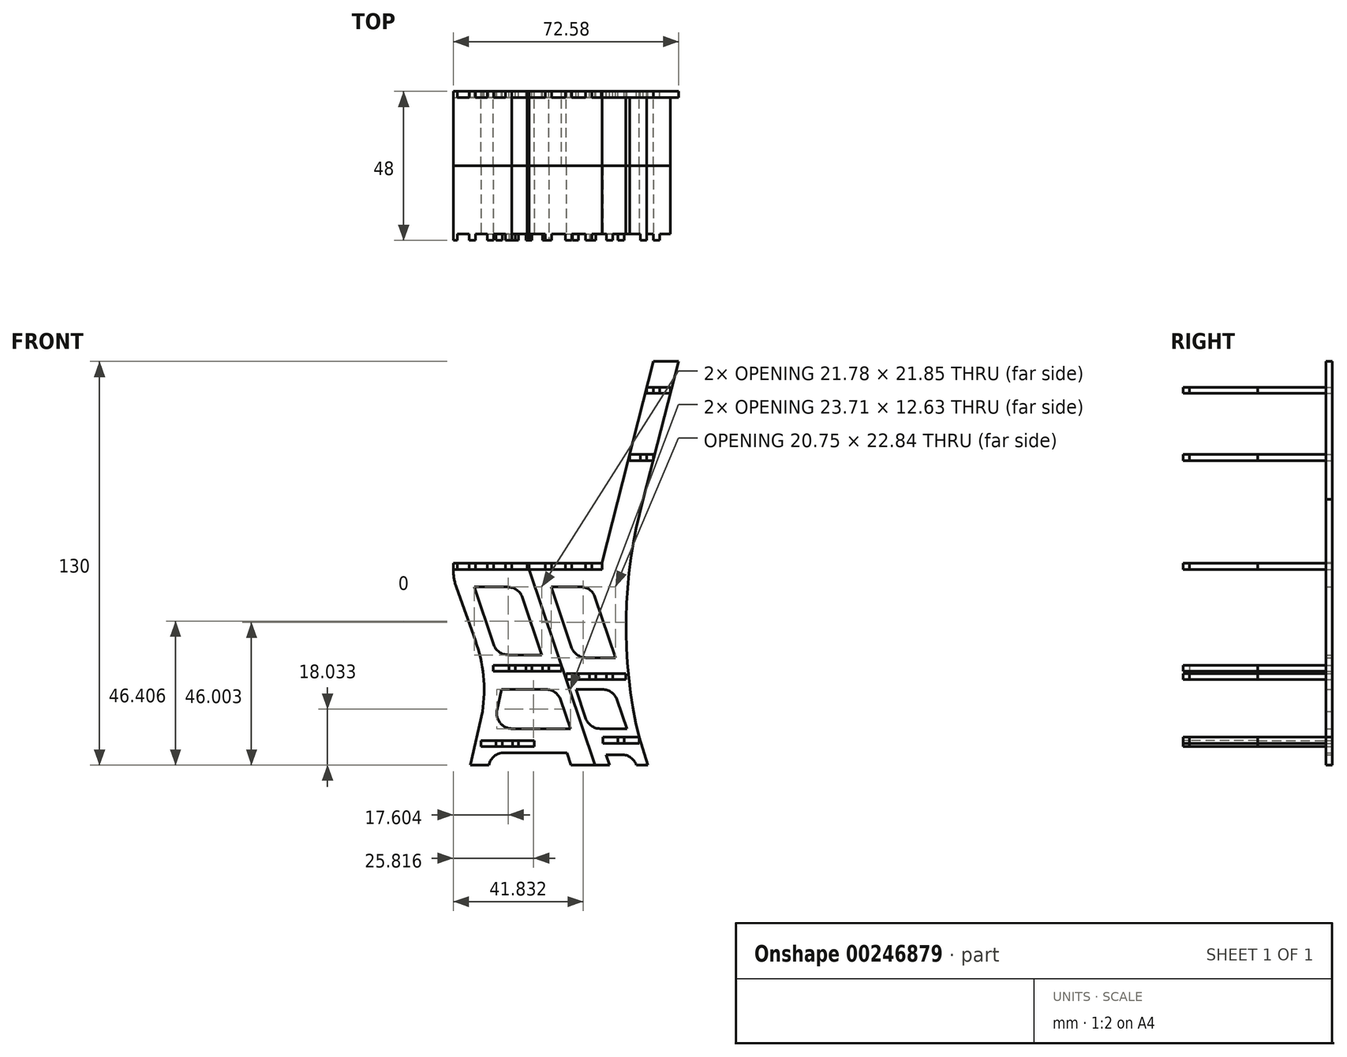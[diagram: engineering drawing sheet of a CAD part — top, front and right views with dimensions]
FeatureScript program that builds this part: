
annotation { "Feature Type Name" : "Feature", "Feature Type Description" : "" }
export const myFeature = defineFeature(function(context is Context, id is Id, definition is map)
    precondition{}
    {
        {
            var Q0;
            Q0=qCreatedBy(makeId("Front.planeOp"),FACE);
            var sketch = newSketch(context, id + "F0", { "sketchPlane" : qUnion([Q0])});
            skLineSegment(sketch, "E0", {"start": v(104.8, -15.97) * mm, "end": v(120.66, 46.4) * mm});
            skLineSegment(sketch, "E1", {"start": v(120.66, 46.4) * mm, "end": v(128.86, 46.4) * mm});
            skLineSegment(sketch, "E2", {"start": v(128.86, 46.4) * mm, "end": v(116.21, -2.66) * mm});
            skLineSegment(sketch, "E3", {"start": v(116.07, -74.61) * mm, "end": v(119.28, -84.78) * mm});
            skLineSegment(sketch, "E4", {"start": v(126.58, -83.6) * mm, "end": v(61.72, -83.6) * mm});
            skLineSegment(sketch, "E5", {"start": v(61.72, -83.6) * mm, "end": v(65.63, -66.38) * mm});
            skLineSegment(sketch, "E6", {"start": v(63.65, -44.37) * mm, "end": v(57.26, -26.44) * mm});
            skLineSegment(sketch, "E7", {"start": v(80.01, -18.6) * mm, "end": v(101.88, -83.6) * mm});
            skLineSegment(sketch, "E8.bottom", {"start": v(74.23, -51.43) * mm, "end": v(76.23, -51.43) * mm});
            skLineSegment(sketch, "E8.top", {"start": v(74.23, -53.43) * mm, "end": v(76.23, -53.43) * mm});
            skLineSegment(sketch, "E8.left", {"start": v(74.23, -51.43) * mm, "end": v(74.23, -53.43) * mm});
            skLineSegment(sketch, "E8.right", {"start": v(76.23, -51.43) * mm, "end": v(76.23, -53.43) * mm});
            skLineSegment(sketch, "E9.1.0.0", {"start": v(79.63, -53.43) * mm, "end": v(81.63, -53.43) * mm});
            skLineSegment(sketch, "E9.1.0.1", {"start": v(79.63, -51.43) * mm, "end": v(79.63, -53.43) * mm});
            skLineSegment(sketch, "E9.1.0.2", {"start": v(79.63, -51.43) * mm, "end": v(81.63, -51.43) * mm});
            skLineSegment(sketch, "E9.1.0.3", {"start": v(81.63, -51.43) * mm, "end": v(81.63, -53.43) * mm});
            skLineSegment(sketch, "E9.2.0.0", {"start": v(85.03, -53.43) * mm, "end": v(87.03, -53.43) * mm});
            skLineSegment(sketch, "E9.2.0.1", {"start": v(85.03, -51.43) * mm, "end": v(85.03, -53.43) * mm});
            skLineSegment(sketch, "E9.2.0.2", {"start": v(85.03, -51.43) * mm, "end": v(87.03, -51.43) * mm});
            skLineSegment(sketch, "E9.2.0.3", {"start": v(87.03, -51.43) * mm, "end": v(87.03, -53.43) * mm});
            skLineSegment(sketch, "E9.direction1", {"start": v(74.23, -53.43) * mm, "end": v(79.63, -53.43) * mm, "construction": true});
            skLineSegment(sketch, "E10.left", {"start": v(94.61, -54.11) * mm, "end": v(94.61, -56.11) * mm});
            skLineSegment(sketch, "E10.right", {"start": v(96.61, -54.11) * mm, "end": v(96.61, -56.11) * mm});
            skLineSegment(sketch, "E11.bottom", {"start": v(69.98, -75.7) * mm, "end": v(71.98, -75.7) * mm});
            skLineSegment(sketch, "E11.top", {"start": v(69.98, -77.7) * mm, "end": v(71.98, -77.7) * mm});
            skLineSegment(sketch, "E11.left", {"start": v(69.98, -75.7) * mm, "end": v(69.98, -77.7) * mm});
            skLineSegment(sketch, "E11.right", {"start": v(71.98, -75.7) * mm, "end": v(71.98, -77.7) * mm});
            skLineSegment(sketch, "E12.1.0.0", {"start": v(75.28, -75.7) * mm, "end": v(75.28, -77.7) * mm});
            skLineSegment(sketch, "E12.1.0.1", {"start": v(75.28, -75.7) * mm, "end": v(77.28, -75.7) * mm});
            skLineSegment(sketch, "E12.1.0.2", {"start": v(77.28, -75.7) * mm, "end": v(77.28, -77.7) * mm});
            skLineSegment(sketch, "E12.1.0.3", {"start": v(75.28, -77.7) * mm, "end": v(77.28, -77.7) * mm});
            skLineSegment(sketch, "E12.direction1", {"start": v(69.98, -77.7) * mm, "end": v(75.28, -77.7) * mm, "construction": true});
            skLineSegment(sketch, "E13.bottom", {"start": v(109.26, -74.61) * mm, "end": v(111.26, -74.61) * mm});
            skLineSegment(sketch, "E13.top", {"start": v(109.26, -76.61) * mm, "end": v(111.26, -76.61) * mm});
            skLineSegment(sketch, "E14.1.0.0", {"start": v(100.11, -54.11) * mm, "end": v(100.11, -56.11) * mm});
            skLineSegment(sketch, "E14.1.0.1", {"start": v(102.11, -54.11) * mm, "end": v(102.11, -56.11) * mm});
            skLineSegment(sketch, "E14.1.0.2", {"start": v(92.81, -56.11) * mm, "end": v(94.81, -56.11) * mm});
            skLineSegment(sketch, "E14.1.0.3", {"start": v(92.81, -54.11) * mm, "end": v(94.81, -54.11) * mm});
            skLineSegment(sketch, "E14.2.0.0", {"start": v(105.61, -54.11) * mm, "end": v(105.61, -56.11) * mm});
            skLineSegment(sketch, "E14.2.0.1", {"start": v(107.61, -54.11) * mm, "end": v(107.61, -56.11) * mm});
            skLineSegment(sketch, "E14.2.0.2", {"start": v(98.31, -56.11) * mm, "end": v(100.31, -56.11) * mm});
            skLineSegment(sketch, "E14.2.0.3", {"start": v(98.31, -54.11) * mm, "end": v(100.31, -54.11) * mm});
            skLineSegment(sketch, "E15.1.0.1", {"start": v(55.63, -20.6) * mm, "end": v(57.63, -20.6) * mm});
            skLineSegment(sketch, "E15.1.0.2", {"start": v(57.63, -18.6) * mm, "end": v(57.63, -20.6) * mm});
            skLineSegment(sketch, "E15.2.0.0", {"start": v(61.43, -18.6) * mm, "end": v(61.43, -20.6) * mm});
            skLineSegment(sketch, "E15.2.0.1", {"start": v(61.43, -20.6) * mm, "end": v(63.43, -20.6) * mm});
            skLineSegment(sketch, "E15.2.0.2", {"start": v(63.43, -18.6) * mm, "end": v(63.43, -20.6) * mm});
            skLineSegment(sketch, "E15.3.0.0", {"start": v(67.23, -18.6) * mm, "end": v(67.23, -20.6) * mm});
            skLineSegment(sketch, "E15.3.0.1", {"start": v(67.23, -20.6) * mm, "end": v(69.23, -20.6) * mm});
            skLineSegment(sketch, "E15.3.0.2", {"start": v(69.23, -18.6) * mm, "end": v(69.23, -20.6) * mm});
            skLineSegment(sketch, "E16.bottom", {"start": v(73.03, -18.6) * mm, "end": v(75.03, -18.6) * mm});
            skLineSegment(sketch, "E16.top", {"start": v(73.03, -20.6) * mm, "end": v(75.03, -20.6) * mm});
            skLineSegment(sketch, "E16.left", {"start": v(73.03, -18.6) * mm, "end": v(73.03, -20.6) * mm});
            skLineSegment(sketch, "E16.right", {"start": v(75.03, -18.6) * mm, "end": v(75.03, -20.6) * mm});
            skLineSegment(sketch, "E17.1.0.1", {"start": v(79.48, -20.6) * mm, "end": v(81.48, -20.6) * mm});
            skLineSegment(sketch, "E17.2.0.0", {"start": v(85.94, -18.6) * mm, "end": v(85.94, -20.6) * mm});
            skLineSegment(sketch, "E17.2.0.1", {"start": v(85.94, -20.6) * mm, "end": v(87.94, -20.6) * mm});
            skLineSegment(sketch, "E17.2.0.2", {"start": v(87.94, -18.6) * mm, "end": v(87.94, -20.6) * mm});
            skLineSegment(sketch, "E17.3.0.0", {"start": v(92.4, -18.6) * mm, "end": v(92.4, -20.6) * mm});
            skLineSegment(sketch, "E17.3.0.1", {"start": v(92.4, -20.6) * mm, "end": v(94.4, -20.6) * mm});
            skLineSegment(sketch, "E17.3.0.2", {"start": v(94.4, -18.6) * mm, "end": v(94.4, -20.6) * mm});
            skLineSegment(sketch, "E17.4.0.0", {"start": v(98.85, -18.6) * mm, "end": v(98.85, -20.6) * mm});
            skLineSegment(sketch, "E17.4.0.1", {"start": v(98.85, -20.6) * mm, "end": v(100.85, -20.6) * mm});
            skLineSegment(sketch, "E17.4.0.2", {"start": v(100.85, -18.57) * mm, "end": v(100.85, -20.6) * mm});
            skLineSegment(sketch, "E17.direction1", {"start": v(73.03, -20.6) * mm, "end": v(79.48, -20.6) * mm, "construction": true});
            skPoint(sketch, "E18.visualSharp", {"position": v(104.13, -18.6) * mm});
            skArc(sketch, "E18.filletArc", {"start": v(100.24, -18.6) * mm, "mid": v(100.55, -18.6) * mm, "end": v(100.85, -18.57) * mm});
            skPoint(sketch, "E19.orphan", {"position": v(100.85, -18.6) * mm});
            skLineSegment(sketch, "E20.bottom", {"start": v(116.51, 16.45) * mm, "end": v(118.51, 16.45) * mm, "construction": true});
            skLineSegment(sketch, "E20.top", {"start": v(116.51, 14.45) * mm, "end": v(118.51, 14.45) * mm, "construction": true});
            skLineSegment(sketch, "E20.left", {"start": v(116.51, 16.45) * mm, "end": v(116.51, 14.45) * mm});
            skLineSegment(sketch, "E20.right", {"start": v(118.51, 16.45) * mm, "end": v(118.51, 14.45) * mm});
            skLineSegment(sketch, "E21.bottom", {"start": v(120.66, 38.08) * mm, "end": v(122.66, 38.08) * mm});
            skLineSegment(sketch, "E21.top", {"start": v(120.66, 36.08) * mm, "end": v(122.66, 36.08) * mm});
            skLineSegment(sketch, "E21.left", {"start": v(120.66, 38.08) * mm, "end": v(120.66, 36.08) * mm});
            skLineSegment(sketch, "E21.right", {"start": v(122.66, 38.08) * mm, "end": v(122.66, 36.08) * mm});
            skLineSegment(sketch, "E22", {"start": v(55.18, -20.6) * mm, "end": v(104.13, -20.6) * mm});
            skLineSegment(sketch, "E23", {"start": v(104.13, -20.6) * mm, "end": v(104.13, -18.6) * mm});
            skLineSegment(sketch, "E24", {"start": v(100.24, -18.6) * mm, "end": v(104.13, -18.6) * mm});
            skLineSegment(sketch, "E25", {"start": v(91.06, -51.43) * mm, "end": v(74.23, -51.43) * mm});
            skLineSegment(sketch, "E26", {"start": v(69.09, -53.43) * mm, "end": v(91.06, -53.43) * mm});
            skLineSegment(sketch, "E27", {"start": v(92.63, -54.11) * mm, "end": v(111.76, -54.11) * mm});
            skLineSegment(sketch, "E28", {"start": v(92.63, -56.11) * mm, "end": v(111.76, -56.11) * mm});
            skLineSegment(sketch, "E29.bottom", {"start": v(65.2, -75.7) * mm, "end": v(82.27, -75.7) * mm});
            skLineSegment(sketch, "E29.top", {"start": v(65.2, -77.7) * mm, "end": v(82.27, -77.7) * mm});
            skLineSegment(sketch, "E29.left", {"start": v(65.2, -75.7) * mm, "end": v(65.2, -77.7) * mm});
            skLineSegment(sketch, "E29.right", {"start": v(82.27, -75.7) * mm, "end": v(82.27, -77.7) * mm});
            skLineSegment(sketch, "E30", {"start": v(69.09, -51.43) * mm, "end": v(69.09, -53.43) * mm});
            skLineSegment(sketch, "E31", {"start": v(111.76, -54.11) * mm, "end": v(111.76, -56.11) * mm});
            skLineSegment(sketch, "E32", {"start": v(116.07, -74.61) * mm, "end": v(104.49, -74.61) * mm});
            skPoint(sketch, "E32.endSnap0", {"position": v(110.26, -74.61) * mm});
            skLineSegment(sketch, "E33", {"start": v(104.49, -74.61) * mm, "end": v(104.49, -76.61) * mm});
            skLineSegment(sketch, "E34", {"start": v(104.49, -76.61) * mm, "end": v(116.07, -76.61) * mm});
            skLineSegment(sketch, "E35", {"start": v(74.23, -51.43) * mm, "end": v(69.09, -51.43) * mm});
            skPoint(sketch, "E36.orphan", {"position": v(59.58, -53.43) * mm});
            skLineSegment(sketch, "E37", {"start": v(108.48, -49.03) * mm, "end": v(99.02, -49.03) * mm});
            skLineSegment(sketch, "E38", {"start": v(94.28, -45.62) * mm, "end": v(87.74, -26.18) * mm});
            skLineSegment(sketch, "E39", {"start": v(87.74, -26.18) * mm, "end": v(97.2, -26.18) * mm});
            skLineSegment(sketch, "E40", {"start": v(101.94, -29.59) * mm, "end": v(108.48, -49.03) * mm});
            skPoint(sketch, "E41.visualSharp", {"position": v(100.8, -26.18) * mm});
            skArc(sketch, "E41.filletArc", {"start": v(101.94, -29.59) * mm, "mid": v(100.12, -27.12) * mm, "end": v(97.2, -26.18) * mm});
            skPoint(sketch, "E42.visualSharp", {"position": v(95.43, -49.03) * mm});
            skArc(sketch, "E42.filletArc", {"start": v(94.28, -45.62) * mm, "mid": v(96.1, -48.09) * mm, "end": v(99.02, -49.03) * mm});
            skLineSegment(sketch, "E43", {"start": v(84.77, -48.13) * mm, "end": v(73.94, -48.13) * mm});
            skLineSegment(sketch, "E44", {"start": v(69.2, -44.72) * mm, "end": v(63, -26.28) * mm});
            skLineSegment(sketch, "E45", {"start": v(63, -26.28) * mm, "end": v(73.83, -26.28) * mm});
            skLineSegment(sketch, "E46", {"start": v(78.57, -29.69) * mm, "end": v(84.77, -48.13) * mm});
            skArc(sketch, "E47.filletArc", {"start": v(78.57, -29.69) * mm, "mid": v(76.75, -27.22) * mm, "end": v(73.83, -26.28) * mm});
            skArc(sketch, "E48.filletArc", {"start": v(69.2, -44.72) * mm, "mid": v(71.02, -47.19) * mm, "end": v(73.94, -48.13) * mm});
            skLineSegment(sketch, "E49", {"start": v(110.48, -80.26) * mm, "end": v(105.45, -80.26) * mm});
            skLineSegment(sketch, "E50", {"start": v(105.45, -80.26) * mm, "end": v(106.64, -83.6) * mm});
            skPoint(sketch, "E51.visualSharp", {"position": v(111.89, -80.26) * mm});
            skArc(sketch, "E51.filletArc", {"start": v(115.43, -85.97) * mm, "mid": v(114.26, -81.98) * mm, "end": v(110.48, -80.26) * mm});
            skLineSegment(sketch, "E52", {"start": v(95.75, -59.26) * mm, "end": v(104.29, -59.26) * mm});
            skArc(sketch, "E53.filletArc", {"start": v(109.03, -62.67) * mm, "mid": v(107.2, -60.2) * mm, "end": v(104.29, -59.26) * mm});
            skLineSegment(sketch, "E54", {"start": v(112.13, -71.9) * mm, "end": v(103.59, -71.9) * mm});
            skLineSegment(sketch, "E55", {"start": v(109.03, -62.67) * mm, "end": v(112.13, -71.9) * mm});
            skLineSegment(sketch, "E56", {"start": v(98.85, -68.49) * mm, "end": v(95.75, -59.26) * mm});
            skPoint(sketch, "E57.visualSharp", {"position": v(100, -71.9) * mm});
            skArc(sketch, "E57.filletArc", {"start": v(98.85, -68.49) * mm, "mid": v(100.67, -70.95) * mm, "end": v(103.59, -71.9) * mm});
            skLineSegment(sketch, "E58", {"start": v(92.81, -79.65) * mm, "end": v(72.62, -79.65) * mm});
            skLineSegment(sketch, "E59", {"start": v(92.81, -79.65) * mm, "end": v(94.15, -83.6) * mm});
            skPoint(sketch, "E60.visualSharp", {"position": v(60.32, -80.23) * mm});
            skArc(sketch, "E60.filletArc", {"start": v(72.62, -79.65) * mm, "mid": v(69.47, -80.76) * mm, "end": v(67.73, -83.6) * mm});
            skLineSegment(sketch, "E61", {"start": v(93.95, -71.9) * mm, "end": v(75.24, -71.9) * mm});
            skLineSegment(sketch, "E62", {"start": v(86.1, -59.26) * mm, "end": v(71.85, -59.26) * mm});
            skLineSegment(sketch, "E63", {"start": v(71.85, -59.26) * mm, "end": v(70.37, -65.78) * mm});
            skLineSegment(sketch, "E64", {"start": v(93.95, -71.9) * mm, "end": v(90.85, -62.67) * mm});
            skPoint(sketch, "E65.visualSharp", {"position": v(82.4, -59.26) * mm});
            skArc(sketch, "E65.filletArc", {"start": v(90.85, -62.67) * mm, "mid": v(89.03, -60.2) * mm, "end": v(86.1, -59.26) * mm});
            skPoint(sketch, "E66.visualSharp", {"position": v(61.68, -71.9) * mm});
            skArc(sketch, "E66.filletArc", {"start": v(70.37, -65.78) * mm, "mid": v(71.33, -70.01) * mm, "end": v(75.24, -71.9) * mm});
            skLineSegment(sketch, "E67", {"start": v(92.63, -56.11) * mm, "end": v(92.63, -54.11) * mm});
            skLineSegment(sketch, "E68", {"start": v(91.06, -51.43) * mm, "end": v(91.06, -53.43) * mm});
            skPoint(sketch, "E69.orphan", {"position": v(91.96, -54.11) * mm});
            skLineSegment(sketch, "E70", {"start": v(116.07, -74.61) * mm, "end": v(116.07, -76.61) * mm});
            skLineSegment(sketch, "E71", {"start": v(120.88, 15.45) * mm, "end": v(112.8, 15.45) * mm, "construction": true});
            skPoint(sketch, "E71.startSnap0", {"position": v(118.51, 15.45) * mm});
            skLineSegment(sketch, "E72.bottom", {"start": v(120.62, 14.45) * mm, "end": v(113.05, 14.45) * mm});
            skLineSegment(sketch, "E72.top", {"start": v(120.62, 16.45) * mm, "end": v(113.05, 16.45) * mm});
            skLineSegment(sketch, "E72.left", {"start": v(120.62, 14.45) * mm, "end": v(120.62, 16.45) * mm});
            skLineSegment(sketch, "E72.right", {"start": v(113.05, 14.45) * mm, "end": v(113.05, 16.45) * mm});
            skPoint(sketch, "E73.oppositeSnap0", {"position": v(121.66, 38.08) * mm});
            skLineSegment(sketch, "E73.bottom", {"start": v(126.2, 36.08) * mm, "end": v(118.55, 36.08) * mm});
            skLineSegment(sketch, "E73.top", {"start": v(126.2, 38.08) * mm, "end": v(118.55, 38.08) * mm});
            skLineSegment(sketch, "E73.left", {"start": v(126.2, 36.08) * mm, "end": v(126.2, 38.08) * mm});
            skLineSegment(sketch, "E73.right", {"start": v(118.55, 36.08) * mm, "end": v(118.55, 38.08) * mm});
            skLineSegment(sketch, "E74", {"start": v(111.26, -74.61) * mm, "end": v(111.26, -76.61) * mm});
            skLineSegment(sketch, "E75", {"start": v(109.26, -74.61) * mm, "end": v(109.26, -76.61) * mm});
            skPoint(sketch, "E76.orphan", {"position": v(100, -84.78) * mm});
            skArc(sketch, "E77", {"start": v(117.4, 1.97) * mm, "mid": v(111.92, -36.24) * mm, "end": v(116.07, -74.61) * mm});
            skPoint(sketch, "E78.orphan", {"position": v(105.95, -42.46) * mm});
            skArc(sketch, "E79", {"start": v(65.63, -66.38) * mm, "mid": v(65.94, -54.82) * mm, "end": v(63.36, -43.54) * mm});
            skLineSegment(sketch, "E80.trimOffspring", {"start": v(54.47, -18.6) * mm, "end": v(100.24, -18.6) * mm});
            skLineSegment(sketch, "E81.trimOffspring", {"start": v(55.18, -20.6) * mm, "end": v(55.63, -20.6) * mm, "construction": true});
            skPoint(sketch, "E82.start.orphan", {"position": v(47.88, -20.6) * mm});
            skPoint(sketch, "E83.start.orphan", {"position": v(41.93, -18.6) * mm});
            skPoint(sketch, "E84.top.start.orphan", {"position": v(49.83, -20.6) * mm});
            skLineSegment(sketch, "E85", {"start": v(80.68, -20.6) * mm, "end": v(80.68, -18.6) * mm});
            skLineSegment(sketch, "E86", {"start": v(80.01, -18.6) * mm, "end": v(80.01, -20.6) * mm});
            skLineSegment(sketch, "E87", {"start": v(56.28, -18.6) * mm, "end": v(56.28, -20.74) * mm});
            skLineSegment(sketch, "E88", {"start": v(104.8, -15.97) * mm, "end": v(104.2, -18.33) * mm});
            skArc(sketch, "E89", {"start": v(103.91, -18.6) * mm, "mid": v(104.1, -18.49) * mm, "end": v(104.21, -18.28) * mm});
            skPoint(sketch, "E90.newPointB", {"position": v(54.47, -18.6) * mm});
            skArc(sketch, "E90.filletArc", {"start": v(56.28, -20.74) * mm, "mid": v(56.52, -23.63) * mm, "end": v(57.26, -26.44) * mm});
            skSolve(sketch);
        }
        {
            var Q0;
            {var subQ12=sQuery(id+"F0.wireOp",EDGE,"E5");Q0=makeQuery(id+"F0.imprint","IMPRINT",FACE,{"disambiguationData":[TD([[makeQuery(id+"F0.imprint","IMPRINT",EDGE,{"derivedFrom":subQ12}),-1.0]])]});}
            var Q1;
            {var subQ3=sQuery(id+"F0.wireOp",EDGE,"E84.left");Q1=makeQuery(id+"F0.imprint","IMPRINT",FACE,{"disambiguationData":[TD([[makeQuery(id+"F0.imprint","IMPRINT",EDGE,{"derivedFrom":subQ3}),-1.0]])]});}
            var Q2;
            {var subQ0=sQuery(id+"F0.wireOp",EDGE,"E84.right");Q2=makeQuery(id+"F0.imprint","IMPRINT",FACE,{"disambiguationData":[TD([[makeQuery(id+"F0.imprint","IMPRINT",EDGE,{"derivedFrom":subQ0}),1.0]])]});}
            var Q3;
            {var subQ0=sQuery(id+"F0.wireOp",EDGE,"E15.1.0.2");Q3=makeQuery(id+"F0.imprint","IMPRINT",FACE,{"disambiguationData":[TD([[makeQuery(id+"F0.imprint","IMPRINT",EDGE,{"derivedFrom":subQ0}),1.0]])]});}
            var Q4;
            {var subQ0=sQuery(id+"F0.wireOp",EDGE,"E15.2.0.2");Q4=makeQuery(id+"F0.imprint","IMPRINT",FACE,{"disambiguationData":[TD([[makeQuery(id+"F0.imprint","IMPRINT",EDGE,{"derivedFrom":subQ0}),1.0]])]});}
            var Q5;
            {var subQ3=sQuery(id+"F0.wireOp",EDGE,"E15.3.0.2");Q5=makeQuery(id+"F0.imprint","IMPRINT",FACE,{"disambiguationData":[TD([[makeQuery(id+"F0.imprint","IMPRINT",EDGE,{"derivedFrom":subQ3}),1.0]])]});}
            var Q6;
            {var subQ0=sQuery(id+"F0.wireOp",EDGE,"E8.left");Q6=makeQuery(id+"F0.imprint","IMPRINT",FACE,{"disambiguationData":[TD([[makeQuery(id+"F0.imprint","IMPRINT",EDGE,{"derivedFrom":subQ0}),-1.0]])]});}
            var Q7;
            {var subQ0=sQuery(id+"F0.wireOp",EDGE,"E8.right");Q7=makeQuery(id+"F0.imprint","IMPRINT",FACE,{"disambiguationData":[TD([[makeQuery(id+"F0.imprint","IMPRINT",EDGE,{"derivedFrom":subQ0}),1.0]])]});}
            var Q8;
            {var subQ0=sQuery(id+"F0.wireOp",EDGE,"E9.1.0.3");Q8=makeQuery(id+"F0.imprint","IMPRINT",FACE,{"disambiguationData":[TD([[makeQuery(id+"F0.imprint","IMPRINT",EDGE,{"derivedFrom":subQ0}),1.0]])]});}
            var Q9;
            {var subQ0=sQuery(id+"F0.wireOp",EDGE,"E9.2.0.3");Q9=makeQuery(id+"F0.imprint","IMPRINT",FACE,{"disambiguationData":[TD([[makeQuery(id+"F0.imprint","IMPRINT",EDGE,{"derivedFrom":subQ0}),1.0]])]});}
            var Q10;
            {var subQ0=sQuery(id+"F0.wireOp",EDGE,"E12.1.0.2");Q10=makeQuery(id+"F0.imprint","IMPRINT",FACE,{"disambiguationData":[TD([[makeQuery(id+"F0.imprint","IMPRINT",EDGE,{"derivedFrom":subQ0}),1.0]])]});}
            var Q11;
            {var subQ0=sQuery(id+"F0.wireOp",EDGE,"E11.right");Q11=makeQuery(id+"F0.imprint","IMPRINT",FACE,{"disambiguationData":[TD([[makeQuery(id+"F0.imprint","IMPRINT",EDGE,{"derivedFrom":subQ0}),1.0]])]});}
            var Q12;
            {var subQ0=sQuery(id+"F0.wireOp",EDGE,"E11.left");Q12=makeQuery(id+"F0.imprint","IMPRINT",FACE,{"disambiguationData":[TD([[makeQuery(id+"F0.imprint","IMPRINT",EDGE,{"derivedFrom":subQ0}),-1.0]])]});}
            var Q13;
            {var subQ0=sQuery(id+"F0.wireOp",EDGE,"E16.right");Q13=makeQuery(id+"F0.imprint","IMPRINT",FACE,{"disambiguationData":[TD([[makeQuery(id+"F0.imprint","IMPRINT",EDGE,{"derivedFrom":subQ0}),1.0]])]});}
            extrude(context, id + "F1", {"entities" : qUnion([Q0, Q1, Q2, Q3, Q4, Q5, Q6, Q7, Q8, Q9, Q10, Q11, Q12, Q13]), "depth" : 2 * mm});
        }
        {
            var Q0;
            {var subQ1=sQuery(id+"F0.wireOp",EDGE,"E0");Q0=makeQuery(id+"F0.imprint","IMPRINT",FACE,{"disambiguationData":[TD([[makeQuery(id+"F0.imprint","IMPRINT",EDGE,{"derivedFrom":subQ1}),-1.0]])]});}
            var Q1;
            {var subQ3=sQuery(id+"F0.wireOp",EDGE,"E16.left");Q1=makeQuery(id+"F0.imprint","IMPRINT",FACE,{"disambiguationData":[TD([[makeQuery(id+"F0.imprint","IMPRINT",EDGE,{"derivedFrom":subQ3}),-1.0]])]});}
            var Q2;
            {var subQ0=sQuery(id+"F0.wireOp",EDGE,"E17.1.0.2");Q2=makeQuery(id+"F0.imprint","IMPRINT",FACE,{"disambiguationData":[TD([[makeQuery(id+"F0.imprint","IMPRINT",EDGE,{"derivedFrom":subQ0}),1.0]])]});}
            var Q3;
            {var subQ0=sQuery(id+"F0.wireOp",EDGE,"E17.2.0.2");Q3=makeQuery(id+"F0.imprint","IMPRINT",FACE,{"disambiguationData":[TD([[makeQuery(id+"F0.imprint","IMPRINT",EDGE,{"derivedFrom":subQ0}),1.0]])]});}
            var Q4;
            {var subQ0=sQuery(id+"F0.wireOp",EDGE,"E17.3.0.2");Q4=makeQuery(id+"F0.imprint","IMPRINT",FACE,{"disambiguationData":[TD([[makeQuery(id+"F0.imprint","IMPRINT",EDGE,{"derivedFrom":subQ0}),1.0]])]});}
            var Q5;
            {var subQ5=sQuery(id+"F0.wireOp",EDGE,"E23");Q5=makeQuery(id+"F0.imprint","IMPRINT",FACE,{"disambiguationData":[TD([[makeQuery(id+"F0.imprint","IMPRINT",EDGE,{"derivedFrom":subQ5}),1.0]])]});}
            var Q6;
            {var subQ1=sQuery(id+"F0.wireOp",EDGE,"E10.left");Q6=makeQuery(id+"F0.imprint","IMPRINT",FACE,{"disambiguationData":[TD([[makeQuery(id+"F0.imprint","IMPRINT",EDGE,{"derivedFrom":subQ1}),-1.0]])]});}
            var Q7;
            {var subQ0=sQuery(id+"F0.wireOp",EDGE,"E10.right");Q7=makeQuery(id+"F0.imprint","IMPRINT",FACE,{"disambiguationData":[TD([[makeQuery(id+"F0.imprint","IMPRINT",EDGE,{"derivedFrom":subQ0}),1.0]])]});}
            var Q8;
            {var subQ0=sQuery(id+"F0.wireOp",EDGE,"E14.1.0.1");Q8=makeQuery(id+"F0.imprint","IMPRINT",FACE,{"disambiguationData":[TD([[makeQuery(id+"F0.imprint","IMPRINT",EDGE,{"derivedFrom":subQ0}),1.0]])]});}
            var Q9;
            {var subQ0=sQuery(id+"F0.wireOp",EDGE,"E14.2.0.1");Q9=makeQuery(id+"F0.imprint","IMPRINT",FACE,{"disambiguationData":[TD([[makeQuery(id+"F0.imprint","IMPRINT",EDGE,{"derivedFrom":subQ0}),1.0]])]});}
            var Q10;
            {var subQ0=sQuery(id+"F0.wireOp",EDGE,"E13.left");Q10=makeQuery(id+"F0.imprint","IMPRINT",FACE,{"disambiguationData":[TD([[makeQuery(id+"F0.imprint","IMPRINT",EDGE,{"derivedFrom":subQ0}),-1.0]])]});}
            var Q11;
            {var subQ5=sQuery(id+"F0.wireOp",EDGE,"E13.right");Q11=makeQuery(id+"F0.imprint","IMPRINT",FACE,{"disambiguationData":[TD([[makeQuery(id+"F0.imprint","IMPRINT",EDGE,{"derivedFrom":subQ5}),1.0]])]});}
            var Q12;
            {var subQ59=sQuery(id+"F0.wireOp",EDGE,"E16.top");Q12=makeQuery(id+"F0.imprint","IMPRINT",FACE,{"disambiguationData":[TD([[makeQuery(id+"F0.imprint","IMPRINT",EDGE,{"derivedFrom":subQ59}),-1.0]])]});}
            var Q13;
            {var subQ0=sQuery(id+"F0.wireOp",EDGE,"E21.right");Q13=makeQuery(id+"F0.imprint","IMPRINT",FACE,{"disambiguationData":[TD([[makeQuery(id+"F0.imprint","IMPRINT",EDGE,{"derivedFrom":subQ0}),1.0]])]});}
            var Q14;
            {var subQ0=sQuery(id+"F0.wireOp",EDGE,"E21.left");Q14=makeQuery(id+"F0.imprint","IMPRINT",FACE,{"disambiguationData":[TD([[makeQuery(id+"F0.imprint","IMPRINT",EDGE,{"derivedFrom":subQ0}),-1.0]])]});}
            var Q15;
            {var subQ3=sQuery(id+"F0.wireOp",EDGE,"E72.left");Q15=makeQuery(id+"F0.imprint","IMPRINT",FACE,{"disambiguationData":[TD([[makeQuery(id+"F0.imprint","IMPRINT",EDGE,{"derivedFrom":subQ3}),-1.0]])]});}
            var Q16;
            {var subQ0=sQuery(id+"F0.wireOp",EDGE,"E20.right");Q16=makeQuery(id+"F0.imprint","IMPRINT",FACE,{"disambiguationData":[TD([[makeQuery(id+"F0.imprint","IMPRINT",EDGE,{"derivedFrom":subQ0}),1.0]])]});}
            var Q17;
            {var subQ0=sQuery(id+"F0.wireOp",EDGE,"E20.left");Q17=makeQuery(id+"F0.imprint","IMPRINT",FACE,{"disambiguationData":[TD([[makeQuery(id+"F0.imprint","IMPRINT",EDGE,{"derivedFrom":subQ0}),-1.0]])]});}
            var Q18;
            {var subQ0=sQuery(id+"F0.wireOp",EDGE,"E33");Q18=makeQuery(id+"F0.imprint","IMPRINT",FACE,{"disambiguationData":[TD([[makeQuery(id+"F0.imprint","IMPRINT",EDGE,{"derivedFrom":subQ0}),1.0]])]});}
            var Q19;
            {var subQ48=sQuery(id+"F0.wireOp",EDGE,"E23");Q19=makeQuery(id+"F0.imprint","IMPRINT",FACE,{"disambiguationData":[TD([[makeQuery(id+"F0.imprint","IMPRINT",EDGE,{"derivedFrom":subQ48}),-1.0]])]});}
            var Q20;
            {var subQ0=sQuery(id+"F0.wireOp",EDGE,"E70");Q20=makeQuery(id+"F0.imprint","IMPRINT",FACE,{"disambiguationData":[TD([[makeQuery(id+"F0.imprint","IMPRINT",EDGE,{"derivedFrom":subQ0}),-1.0]])]});}
            var Q21;
            {var subQ1=sQuery(id+"F0.wireOp",EDGE,"E17.2.0.0");Q21=makeQuery(id+"F0.imprint","IMPRINT",FACE,{"disambiguationData":[TD([[makeQuery(id+"F0.imprint","IMPRINT",EDGE,{"derivedFrom":subQ1}),-1.0]])]});}
            extrude(context, id + "F2", {"entities" : qUnion([Q0, Q1, Q2, Q3, Q4, Q5, Q6, Q7, Q8, Q9, Q10, Q11, Q12, Q13, Q14, Q15, Q16, Q17, Q18, Q19, Q20, Q21]), "depth" : 2 * mm});
        }
        {
            var Q0;
            Q0=makeQuery(id+"F0.imprint","IMPRINT",FACE,{"disambiguationData":[TD([[makeQuery(id+"F0.imprint","IMPRINT",EDGE,{"derivedFrom":sQuery(id+"F0.wireOp",EDGE,"E84.bottom")}),-1.0]])]});
            var Q1;
            {var subQ0=sQuery(id+"F0.wireOp",EDGE,"E15.1.0.0");Q1=makeQuery(id+"F0.imprint","IMPRINT",FACE,{"disambiguationData":[TD([[makeQuery(id+"F0.imprint","IMPRINT",EDGE,{"derivedFrom":subQ0}),1.0]])]});}
            var Q2;
            {var subQ0=sQuery(id+"F0.wireOp",EDGE,"E15.2.0.0");Q2=makeQuery(id+"F0.imprint","IMPRINT",FACE,{"disambiguationData":[TD([[makeQuery(id+"F0.imprint","IMPRINT",EDGE,{"derivedFrom":subQ0}),1.0]])]});}
            var Q3;
            {var subQ0=sQuery(id+"F0.wireOp",EDGE,"E15.3.0.0");Q3=makeQuery(id+"F0.imprint","IMPRINT",FACE,{"disambiguationData":[TD([[makeQuery(id+"F0.imprint","IMPRINT",EDGE,{"derivedFrom":subQ0}),1.0]])]});}
            var Q4;
            {var subQ0=sQuery(id+"F0.wireOp",EDGE,"E8.left");Q4=makeQuery(id+"F0.imprint","IMPRINT",FACE,{"disambiguationData":[TD([[makeQuery(id+"F0.imprint","IMPRINT",EDGE,{"derivedFrom":subQ0}),1.0]])]});}
            var Q5;
            {var subQ0=sQuery(id+"F0.wireOp",EDGE,"E9.1.0.1");Q5=makeQuery(id+"F0.imprint","IMPRINT",FACE,{"disambiguationData":[TD([[makeQuery(id+"F0.imprint","IMPRINT",EDGE,{"derivedFrom":subQ0}),1.0]])]});}
            var Q6;
            {var subQ0=sQuery(id+"F0.wireOp",EDGE,"E9.2.0.1");Q6=makeQuery(id+"F0.imprint","IMPRINT",FACE,{"disambiguationData":[TD([[makeQuery(id+"F0.imprint","IMPRINT",EDGE,{"derivedFrom":subQ0}),1.0]])]});}
            var Q7;
            {var subQ0=sQuery(id+"F0.wireOp",EDGE,"E11.left");Q7=makeQuery(id+"F0.imprint","IMPRINT",FACE,{"disambiguationData":[TD([[makeQuery(id+"F0.imprint","IMPRINT",EDGE,{"derivedFrom":subQ0}),1.0]])]});}
            var Q8;
            {var subQ0=sQuery(id+"F0.wireOp",EDGE,"E12.1.0.0");Q8=makeQuery(id+"F0.imprint","IMPRINT",FACE,{"disambiguationData":[TD([[makeQuery(id+"F0.imprint","IMPRINT",EDGE,{"derivedFrom":subQ0}),1.0]])]});}
            var Q9;
            Q9=makeQuery(id+"F0.imprint","IMPRINT",FACE,{"disambiguationData":[TD([[makeQuery(id+"F0.imprint","IMPRINT",EDGE,{"derivedFrom":sQuery(id+"F0.wireOp",EDGE,"E16.bottom")}),-1.0]])]});
            var Q10;
            {var subQ0=sQuery(id+"F0.wireOp",EDGE,"E17.1.0.0");Q10=makeQuery(id+"F0.imprint","IMPRINT",FACE,{"disambiguationData":[TD([[makeQuery(id+"F0.imprint","IMPRINT",EDGE,{"derivedFrom":subQ0}),1.0]])]});}
            var Q11;
            {var subQ0=sQuery(id+"F0.wireOp",EDGE,"E17.2.0.0");Q11=makeQuery(id+"F0.imprint","IMPRINT",FACE,{"disambiguationData":[TD([[makeQuery(id+"F0.imprint","IMPRINT",EDGE,{"derivedFrom":subQ0}),1.0]])]});}
            var Q12;
            {var subQ0=sQuery(id+"F0.wireOp",EDGE,"E17.3.0.0");Q12=makeQuery(id+"F0.imprint","IMPRINT",FACE,{"disambiguationData":[TD([[makeQuery(id+"F0.imprint","IMPRINT",EDGE,{"derivedFrom":subQ0}),1.0]])]});}
            var Q13;
            {var subQ5=sQuery(id+"F0.wireOp",EDGE,"E17.4.0.0");Q13=makeQuery(id+"F0.imprint","IMPRINT",FACE,{"disambiguationData":[TD([[makeQuery(id+"F0.imprint","IMPRINT",EDGE,{"derivedFrom":subQ5}),1.0]])]});}
            var Q14;
            {var subQ0=sQuery(id+"F0.wireOp",EDGE,"E10.left");Q14=makeQuery(id+"F0.imprint","IMPRINT",FACE,{"disambiguationData":[TD([[makeQuery(id+"F0.imprint","IMPRINT",EDGE,{"derivedFrom":subQ0}),1.0]])]});}
            var Q15;
            {var subQ0=sQuery(id+"F0.wireOp",EDGE,"E14.1.0.0");Q15=makeQuery(id+"F0.imprint","IMPRINT",FACE,{"disambiguationData":[TD([[makeQuery(id+"F0.imprint","IMPRINT",EDGE,{"derivedFrom":subQ0}),1.0]])]});}
            var Q16;
            {var subQ0=sQuery(id+"F0.wireOp",EDGE,"E14.2.0.0");Q16=makeQuery(id+"F0.imprint","IMPRINT",FACE,{"disambiguationData":[TD([[makeQuery(id+"F0.imprint","IMPRINT",EDGE,{"derivedFrom":subQ0}),1.0]])]});}
            var Q17;
            {var subQ0=sQuery(id+"F0.wireOp",EDGE,"E13.left");Q17=makeQuery(id+"F0.imprint","IMPRINT",FACE,{"disambiguationData":[TD([[makeQuery(id+"F0.imprint","IMPRINT",EDGE,{"derivedFrom":subQ0}),1.0]])]});}
            var Q18;
            Q18=makeQuery(id+"F0.imprint","IMPRINT",FACE,{"disambiguationData":[TD([[makeQuery(id+"F0.imprint","IMPRINT",EDGE,{"derivedFrom":sQuery(id+"F0.wireOp",EDGE,"E20.bottom")}),-1.0]])]});
            var Q19;
            Q19=makeQuery(id+"F0.imprint","IMPRINT",FACE,{"disambiguationData":[TD([[makeQuery(id+"F0.imprint","IMPRINT",EDGE,{"derivedFrom":sQuery(id+"F0.wireOp",EDGE,"E21.bottom")}),-1.0]])]});
            var Q20;
            {var subQ0=sQuery(id+"F0.wireOp",EDGE,"E20.left");Q20=makeQuery(id+"F0.imprint","IMPRINT",FACE,{"disambiguationData":[TD([[makeQuery(id+"F0.imprint","IMPRINT",EDGE,{"derivedFrom":subQ0}),1.0]])]});}
            var Q21;
            {var subQ0=sQuery(id+"F0.wireOp",EDGE,"E21.left");Q21=makeQuery(id+"F0.imprint","IMPRINT",FACE,{"disambiguationData":[TD([[makeQuery(id+"F0.imprint","IMPRINT",EDGE,{"derivedFrom":subQ0}),1.0]])]});}
            var Q22;
            {var subQ0=sQuery(id+"F0.wireOp",EDGE,"E74");Q22=makeQuery(id+"F0.imprint","IMPRINT",FACE,{"disambiguationData":[TD([[makeQuery(id+"F0.imprint","IMPRINT",EDGE,{"derivedFrom":subQ0}),-1.0]])]});}
            var Q23;
            {var subQ3=sQuery(id+"F0.wireOp",EDGE,"j8O7oxjR-24Yr-Gt1T-WmpP-8T0AMHy3uAnI");Q23=makeQuery(id+"F0.imprint","IMPRINT",FACE,{"disambiguationData":[TD([[makeQuery(id+"F0.imprint","IMPRINT",EDGE,{"derivedFrom":subQ3}),1.0]])]});}
            var Q24;
            {var subQ0=sQuery(id+"F0.wireOp",EDGE,"kYUembHk-8FI4-1AiB-vZVx-KGB4nnve0D11");Q24=makeQuery(id+"F0.imprint","IMPRINT",FACE,{"disambiguationData":[TD([[makeQuery(id+"F0.imprint","IMPRINT",EDGE,{"derivedFrom":subQ0}),1.0]])]});}
            var Q25;
            {var subQ0=sQuery(id+"F0.wireOp",EDGE,"E17.1.0.0");Q25=makeQuery(id+"F0.imprint","IMPRINT",FACE,{"disambiguationData":[TD([[makeQuery(id+"F0.imprint","IMPRINT",EDGE,{"derivedFrom":subQ0}),-1.0]])]});}
            var Q26;
            {var subQ3=sQuery(id+"F0.wireOp",EDGE,"E85");Q26=makeQuery(id+"F0.imprint","IMPRINT",FACE,{"disambiguationData":[TD([[makeQuery(id+"F0.imprint","IMPRINT",EDGE,{"derivedFrom":subQ3}),1.0]])]});}
            var Q27;
            {var subQ0=sQuery(id+"F0.wireOp",EDGE,"E86");Q27=makeQuery(id+"F0.imprint","IMPRINT",FACE,{"disambiguationData":[TD([[makeQuery(id+"F0.imprint","IMPRINT",EDGE,{"derivedFrom":subQ0}),1.0]])]});}
            var Q28;
            {var subQ0=sQuery(id+"F0.wireOp",EDGE,"E15.1.0.0");Q28=makeQuery(id+"F0.imprint","IMPRINT",FACE,{"disambiguationData":[TD([[makeQuery(id+"F0.imprint","IMPRINT",EDGE,{"derivedFrom":subQ0}),-1.0]])]});}
            var Q29;
            {var subQ0=sQuery(id+"F0.wireOp",EDGE,"E16.left");Q29=makeQuery(id+"F0.imprint","IMPRINT",FACE,{"disambiguationData":[TD([[makeQuery(id+"F0.imprint","IMPRINT",EDGE,{"derivedFrom":subQ0}),1.0]])]});}
            var Q30;
            {var subQ0=sQuery(id+"F0.wireOp",EDGE,"E15.1.0.2");Q30=makeQuery(id+"F0.imprint","IMPRINT",FACE,{"disambiguationData":[TD([[makeQuery(id+"F0.imprint","IMPRINT",EDGE,{"derivedFrom":subQ0}),-1.0]])]});}
            extrude(context, id + "F3", {"entities" : qUnion([Q0, Q1, Q2, Q3, Q4, Q5, Q6, Q7, Q8, Q9, Q10, Q11, Q12, Q13, Q14, Q15, Q16, Q17, Q18, Q19, Q20, Q21, Q22, Q23, Q24, Q25, Q26, Q27, Q28, Q29, Q30]), "depth" : 24 * mm});
        }
        {
            var Q0;
            {var subQ3=sQuery(id+"F0.wireOp",EDGE,"E84.left");Q0=makeQuery(id+"F0.imprint","IMPRINT",FACE,{"disambiguationData":[TD([[makeQuery(id+"F0.imprint","IMPRINT",EDGE,{"derivedFrom":subQ3}),-1.0]])]});}
            var Q1;
            {var subQ0=sQuery(id+"F0.wireOp",EDGE,"E84.right");Q1=makeQuery(id+"F0.imprint","IMPRINT",FACE,{"disambiguationData":[TD([[makeQuery(id+"F0.imprint","IMPRINT",EDGE,{"derivedFrom":subQ0}),1.0]])]});}
            var Q2;
            {var subQ0=sQuery(id+"F0.wireOp",EDGE,"E15.1.0.2");Q2=makeQuery(id+"F0.imprint","IMPRINT",FACE,{"disambiguationData":[TD([[makeQuery(id+"F0.imprint","IMPRINT",EDGE,{"derivedFrom":subQ0}),1.0]])]});}
            var Q3;
            {var subQ5=sQuery(id+"F0.wireOp",EDGE,"E23");Q3=makeQuery(id+"F0.imprint","IMPRINT",FACE,{"disambiguationData":[TD([[makeQuery(id+"F0.imprint","IMPRINT",EDGE,{"derivedFrom":subQ5}),1.0]])]});}
            var Q4;
            {var subQ0=sQuery(id+"F0.wireOp",EDGE,"E17.3.0.2");Q4=makeQuery(id+"F0.imprint","IMPRINT",FACE,{"disambiguationData":[TD([[makeQuery(id+"F0.imprint","IMPRINT",EDGE,{"derivedFrom":subQ0}),1.0]])]});}
            var Q5;
            {var subQ0=sQuery(id+"F0.wireOp",EDGE,"E17.2.0.2");Q5=makeQuery(id+"F0.imprint","IMPRINT",FACE,{"disambiguationData":[TD([[makeQuery(id+"F0.imprint","IMPRINT",EDGE,{"derivedFrom":subQ0}),1.0]])]});}
            var Q6;
            {var subQ0=sQuery(id+"F0.wireOp",EDGE,"E17.1.0.2");Q6=makeQuery(id+"F0.imprint","IMPRINT",FACE,{"disambiguationData":[TD([[makeQuery(id+"F0.imprint","IMPRINT",EDGE,{"derivedFrom":subQ0}),1.0]])]});}
            var Q7;
            {var subQ3=sQuery(id+"F0.wireOp",EDGE,"E16.left");Q7=makeQuery(id+"F0.imprint","IMPRINT",FACE,{"disambiguationData":[TD([[makeQuery(id+"F0.imprint","IMPRINT",EDGE,{"derivedFrom":subQ3}),-1.0]])]});}
            var Q8;
            {var subQ0=sQuery(id+"F0.wireOp",EDGE,"E15.2.0.2");Q8=makeQuery(id+"F0.imprint","IMPRINT",FACE,{"disambiguationData":[TD([[makeQuery(id+"F0.imprint","IMPRINT",EDGE,{"derivedFrom":subQ0}),1.0]])]});}
            var Q9;
            {var subQ0=sQuery(id+"F0.wireOp",EDGE,"E9.1.0.3");Q9=makeQuery(id+"F0.imprint","IMPRINT",FACE,{"disambiguationData":[TD([[makeQuery(id+"F0.imprint","IMPRINT",EDGE,{"derivedFrom":subQ0}),1.0]])]});}
            var Q10;
            {var subQ0=sQuery(id+"F0.wireOp",EDGE,"E8.right");Q10=makeQuery(id+"F0.imprint","IMPRINT",FACE,{"disambiguationData":[TD([[makeQuery(id+"F0.imprint","IMPRINT",EDGE,{"derivedFrom":subQ0}),1.0]])]});}
            var Q11;
            {var subQ0=sQuery(id+"F0.wireOp",EDGE,"E8.left");Q11=makeQuery(id+"F0.imprint","IMPRINT",FACE,{"disambiguationData":[TD([[makeQuery(id+"F0.imprint","IMPRINT",EDGE,{"derivedFrom":subQ0}),-1.0]])]});}
            var Q12;
            {var subQ0=sQuery(id+"F0.wireOp",EDGE,"E11.left");Q12=makeQuery(id+"F0.imprint","IMPRINT",FACE,{"disambiguationData":[TD([[makeQuery(id+"F0.imprint","IMPRINT",EDGE,{"derivedFrom":subQ0}),-1.0]])]});}
            var Q13;
            {var subQ0=sQuery(id+"F0.wireOp",EDGE,"E11.right");Q13=makeQuery(id+"F0.imprint","IMPRINT",FACE,{"disambiguationData":[TD([[makeQuery(id+"F0.imprint","IMPRINT",EDGE,{"derivedFrom":subQ0}),1.0]])]});}
            var Q14;
            {var subQ0=sQuery(id+"F0.wireOp",EDGE,"E12.1.0.2");Q14=makeQuery(id+"F0.imprint","IMPRINT",FACE,{"disambiguationData":[TD([[makeQuery(id+"F0.imprint","IMPRINT",EDGE,{"derivedFrom":subQ0}),1.0]])]});}
            var Q15;
            {var subQ0=sQuery(id+"F0.wireOp",EDGE,"E13.left");Q15=makeQuery(id+"F0.imprint","IMPRINT",FACE,{"disambiguationData":[TD([[makeQuery(id+"F0.imprint","IMPRINT",EDGE,{"derivedFrom":subQ0}),-1.0]])]});}
            var Q16;
            {var subQ0=sQuery(id+"F0.wireOp",EDGE,"E14.2.0.1");Q16=makeQuery(id+"F0.imprint","IMPRINT",FACE,{"disambiguationData":[TD([[makeQuery(id+"F0.imprint","IMPRINT",EDGE,{"derivedFrom":subQ0}),1.0]])]});}
            var Q17;
            {var subQ5=sQuery(id+"F0.wireOp",EDGE,"E13.right");Q17=makeQuery(id+"F0.imprint","IMPRINT",FACE,{"disambiguationData":[TD([[makeQuery(id+"F0.imprint","IMPRINT",EDGE,{"derivedFrom":subQ5}),1.0]])]});}
            var Q18;
            {var subQ0=sQuery(id+"F0.wireOp",EDGE,"E14.2.0.0");Q18=makeQuery(id+"F0.imprint","IMPRINT",FACE,{"disambiguationData":[TD([[makeQuery(id+"F0.imprint","IMPRINT",EDGE,{"derivedFrom":subQ0}),1.0]])]});}
            var Q19;
            {var subQ0=sQuery(id+"F0.wireOp",EDGE,"E10.right");Q19=makeQuery(id+"F0.imprint","IMPRINT",FACE,{"disambiguationData":[TD([[makeQuery(id+"F0.imprint","IMPRINT",EDGE,{"derivedFrom":subQ0}),1.0]])]});}
            var Q20;
            {var subQ1=sQuery(id+"F0.wireOp",EDGE,"E10.left");Q20=makeQuery(id+"F0.imprint","IMPRINT",FACE,{"disambiguationData":[TD([[makeQuery(id+"F0.imprint","IMPRINT",EDGE,{"derivedFrom":subQ1}),-1.0]])]});}
            var Q21;
            {var subQ0=sQuery(id+"F0.wireOp",EDGE,"E14.1.0.1");Q21=makeQuery(id+"F0.imprint","IMPRINT",FACE,{"disambiguationData":[TD([[makeQuery(id+"F0.imprint","IMPRINT",EDGE,{"derivedFrom":subQ0}),1.0]])]});}
            var Q22;
            {var subQ0=sQuery(id+"F0.wireOp",EDGE,"E70");Q22=makeQuery(id+"F0.imprint","IMPRINT",FACE,{"disambiguationData":[TD([[makeQuery(id+"F0.imprint","IMPRINT",EDGE,{"derivedFrom":subQ0}),-1.0]])]});}
            var Q23;
            {var subQ0=sQuery(id+"F0.wireOp",EDGE,"E33");Q23=makeQuery(id+"F0.imprint","IMPRINT",FACE,{"disambiguationData":[TD([[makeQuery(id+"F0.imprint","IMPRINT",EDGE,{"derivedFrom":subQ0}),1.0]])]});}
            var Q24;
            {var subQ0=sQuery(id+"F0.wireOp",EDGE,"E16.right");Q24=makeQuery(id+"F0.imprint","IMPRINT",FACE,{"disambiguationData":[TD([[makeQuery(id+"F0.imprint","IMPRINT",EDGE,{"derivedFrom":subQ0}),1.0]])]});}
            extrude(context, id + "F4", {"entities" : qUnion([Q0, Q1, Q2, Q3, Q4, Q5, Q6, Q7, Q8, Q9, Q10, Q11, Q12, Q13, Q14, Q15, Q16, Q17, Q18, Q19, Q20, Q21, Q22, Q23, Q24]), "depth" : 24 * mm, "hasSecondDirection" : true, "secondDirectionOppositeDirection" : false, "secondDirectionDepth" : 2 * mm});
        }
        {
            var Q0;
            {var subQ0=sQuery(id+"F0.wireOp",EDGE,"E9.2.0.3");Q0=makeQuery(id+"F0.imprint","IMPRINT",FACE,{"disambiguationData":[TD([[makeQuery(id+"F0.imprint","IMPRINT",EDGE,{"derivedFrom":subQ0}),1.0]])]});}
            var Q1;
            {var subQ0=sQuery(id+"F0.wireOp",EDGE,"E20.right");Q1=makeQuery(id+"F0.imprint","IMPRINT",FACE,{"disambiguationData":[TD([[makeQuery(id+"F0.imprint","IMPRINT",EDGE,{"derivedFrom":subQ0}),1.0]])]});}
            var Q2;
            {var subQ0=sQuery(id+"F0.wireOp",EDGE,"E20.left");Q2=makeQuery(id+"F0.imprint","IMPRINT",FACE,{"disambiguationData":[TD([[makeQuery(id+"F0.imprint","IMPRINT",EDGE,{"derivedFrom":subQ0}),-1.0]])]});}
            var Q3;
            {var subQ0=sQuery(id+"F0.wireOp",EDGE,"E21.right");Q3=makeQuery(id+"F0.imprint","IMPRINT",FACE,{"disambiguationData":[TD([[makeQuery(id+"F0.imprint","IMPRINT",EDGE,{"derivedFrom":subQ0}),1.0]])]});}
            var Q4;
            {var subQ0=sQuery(id+"F0.wireOp",EDGE,"E21.left");Q4=makeQuery(id+"F0.imprint","IMPRINT",FACE,{"disambiguationData":[TD([[makeQuery(id+"F0.imprint","IMPRINT",EDGE,{"derivedFrom":subQ0}),-1.0]])]});}
            var Q5;
            {var subQ1=sQuery(id+"F0.wireOp",EDGE,"E17.2.0.0");Q5=makeQuery(id+"F0.imprint","IMPRINT",FACE,{"disambiguationData":[TD([[makeQuery(id+"F0.imprint","IMPRINT",EDGE,{"derivedFrom":subQ1}),-1.0]])]});}
            extrude(context, id + "F5", {"entities" : qUnion([Q0, Q1, Q2, Q3, Q4, Q5]), "depth" : 24 * mm, "hasSecondDirection" : true, "secondDirectionOppositeDirection" : false, "secondDirectionDepth" : 2 * mm});
        }
        {
            var Q0;
            Q0=makeQuery(id+"F4.opExtrude","SWEPT_BODY",BODY,{"disambiguationData":[OSD([sQuery(id+"F0.wireOp",EDGE,"E15.1.0.2"),sQuery(id+"F0.wireOp",EDGE,"E15.2.0.0"),sQuery(id+"F0.wireOp",EDGE,"E22"),sQuery(id+"F0.wireOp",EDGE,"E80.trimOffspring")])]});
            var Q1;
            Q1=makeQuery(id+"F4.opExtrude","SWEPT_BODY",BODY,{"disambiguationData":[OSD([sQuery(id+"F0.wireOp",EDGE,"E15.2.0.2"),sQuery(id+"F0.wireOp",EDGE,"E15.3.0.0"),sQuery(id+"F0.wireOp",EDGE,"E22"),sQuery(id+"F0.wireOp",EDGE,"E80.trimOffspring")])]});
            var Q2;
            Q2=makeQuery(id+"F4.opExtrude","SWEPT_BODY",BODY,{"disambiguationData":[OSD([sQuery(id+"F0.wireOp",EDGE,"E15.3.0.2"),sQuery(id+"F0.wireOp",EDGE,"E16.left"),sQuery(id+"F0.wireOp",EDGE,"E22"),sQuery(id+"F0.wireOp",EDGE,"E80.trimOffspring")])]});
            var Q3;
            Q3=makeQuery(id+"F4.opExtrude","SWEPT_BODY",BODY,{"disambiguationData":[OSD([sQuery(id+"F0.wireOp",EDGE,"E17.1.0.2"),sQuery(id+"F0.wireOp",EDGE,"E17.2.0.0"),sQuery(id+"F0.wireOp",EDGE,"E22"),sQuery(id+"F0.wireOp",EDGE,"E80.trimOffspring")])]});
            var Q4;
            Q4=makeQuery(id+"F4.opExtrude","SWEPT_BODY",BODY,{"disambiguationData":[OSD([sQuery(id+"F0.wireOp",EDGE,"E17.2.0.2"),sQuery(id+"F0.wireOp",EDGE,"E17.3.0.0"),sQuery(id+"F0.wireOp",EDGE,"E22"),sQuery(id+"F0.wireOp",EDGE,"E80.trimOffspring")])]});
            var Q5;
            Q5=makeQuery(id+"F4.opExtrude","SWEPT_BODY",BODY,{"disambiguationData":[OSD([sQuery(id+"F0.wireOp",EDGE,"E17.3.0.2"),sQuery(id+"F0.wireOp",EDGE,"E17.4.0.0"),sQuery(id+"F0.wireOp",EDGE,"E22"),sQuery(id+"F0.wireOp",EDGE,"E80.trimOffspring")])]});
            var Q6;
            Q6=makeQuery(id+"F4.opExtrude","SWEPT_BODY",BODY,{"disambiguationData":[OSD([sQuery(id+"F0.wireOp",EDGE,"E17.4.0.2"),sQuery(id+"F0.wireOp",EDGE,"E22"),sQuery(id+"F0.wireOp",EDGE,"E23"),sQuery(id+"F0.wireOp",EDGE,"E24")])]});
            var Q7;
            Q7=makeQuery(id+"F4.opExtrude","SWEPT_BODY",BODY,{"disambiguationData":[OSD([sQuery(id+"F0.wireOp",EDGE,"E15.1.0.2"),sQuery(id+"F0.wireOp",EDGE,"E15.2.0.0"),sQuery(id+"F0.wireOp",EDGE,"E22"),sQuery(id+"F0.wireOp",EDGE,"E80.trimOffspring")])]});
            var Q8;
            Q8=makeQuery(id+"F4.opExtrude","SWEPT_BODY",BODY,{"disambiguationData":[OSD([sQuery(id+"F0.wireOp",EDGE,"E15.2.0.2"),sQuery(id+"F0.wireOp",EDGE,"E15.3.0.0"),sQuery(id+"F0.wireOp",EDGE,"E22"),sQuery(id+"F0.wireOp",EDGE,"E80.trimOffspring")])]});
            var Q9;
            Q9=makeQuery(id+"F4.opExtrude","SWEPT_BODY",BODY,{"disambiguationData":[OSD([sQuery(id+"F0.wireOp",EDGE,"E15.3.0.2"),sQuery(id+"F0.wireOp",EDGE,"E16.left"),sQuery(id+"F0.wireOp",EDGE,"E22"),sQuery(id+"F0.wireOp",EDGE,"E80.trimOffspring")])]});
            var Q10;
            Q10=makeQuery(id+"F4.opExtrude","SWEPT_BODY",BODY,{"disambiguationData":[OSD([sQuery(id+"F0.wireOp",EDGE,"E17.1.0.2"),sQuery(id+"F0.wireOp",EDGE,"E17.2.0.0"),sQuery(id+"F0.wireOp",EDGE,"E22"),sQuery(id+"F0.wireOp",EDGE,"E80.trimOffspring")])]});
            var Q11;
            Q11=makeQuery(id+"F4.opExtrude","SWEPT_BODY",BODY,{"disambiguationData":[OSD([sQuery(id+"F0.wireOp",EDGE,"E17.2.0.2"),sQuery(id+"F0.wireOp",EDGE,"E17.3.0.0"),sQuery(id+"F0.wireOp",EDGE,"E22"),sQuery(id+"F0.wireOp",EDGE,"E80.trimOffspring")])]});
            var Q12;
            Q12=makeQuery(id+"F4.opExtrude","SWEPT_BODY",BODY,{"disambiguationData":[OSD([sQuery(id+"F0.wireOp",EDGE,"E17.3.0.2"),sQuery(id+"F0.wireOp",EDGE,"E17.4.0.0"),sQuery(id+"F0.wireOp",EDGE,"E22"),sQuery(id+"F0.wireOp",EDGE,"E80.trimOffspring")])]});
            var Q13;
            Q13=makeQuery(id+"F4.opExtrude","SWEPT_BODY",BODY,{"disambiguationData":[OSD([sQuery(id+"F0.wireOp",EDGE,"E17.4.0.2"),sQuery(id+"F0.wireOp",EDGE,"E22"),sQuery(id+"F0.wireOp",EDGE,"E23"),sQuery(id+"F0.wireOp",EDGE,"E24")])]});
            var Q14;
            Q14=makeQuery(id+"F3.opExtrude","SWEPT_BODY",BODY,{"disambiguationData":[OSD([sQuery(id+"F0.wireOp",EDGE,"E15.3.0.0"),sQuery(id+"F0.wireOp",EDGE,"E15.3.0.2"),sQuery(id+"F0.wireOp",EDGE,"E22"),sQuery(id+"F0.wireOp",EDGE,"E80.trimOffspring")])]});
            var Q15;
            Q15=makeQuery(id+"F4.opExtrude","SWEPT_BODY",BODY,{"disambiguationData":[OSD([sQuery(id+"F0.wireOp",EDGE,"E11.right"),sQuery(id+"F0.wireOp",EDGE,"E12.1.0.0"),sQuery(id+"F0.wireOp",EDGE,"E29.bottom"),sQuery(id+"F0.wireOp",EDGE,"E29.top")])]});
            var Q16;
            Q16=makeQuery(id+"F4.opExtrude","SWEPT_BODY",BODY,{"disambiguationData":[OSD([sQuery(id+"F0.wireOp",EDGE,"E12.1.0.2"),sQuery(id+"F0.wireOp",EDGE,"E29.bottom"),sQuery(id+"F0.wireOp",EDGE,"E29.top"),sQuery(id+"F0.wireOp",EDGE,"E29.right")])]});
            var Q17;
            Q17=makeQuery(id+"F4.opExtrude","SWEPT_BODY",BODY,{"disambiguationData":[OSD([sQuery(id+"F0.wireOp",EDGE,"E11.left"),sQuery(id+"F0.wireOp",EDGE,"E29.bottom"),sQuery(id+"F0.wireOp",EDGE,"E29.top"),sQuery(id+"F0.wireOp",EDGE,"E29.left")])]});
            var Q18;
            Q18=makeQuery(id+"F3.opExtrude","SWEPT_BODY",BODY,{"disambiguationData":[OSD([sQuery(id+"F0.wireOp",EDGE,"E12.1.0.0"),sQuery(id+"F0.wireOp",EDGE,"E12.1.0.2"),sQuery(id+"F0.wireOp",EDGE,"E29.bottom"),sQuery(id+"F0.wireOp",EDGE,"E29.top")])]});
            var Q19;
            Q19=makeQuery(id+"F3.opExtrude","SWEPT_BODY",BODY,{"disambiguationData":[OSD([sQuery(id+"F0.wireOp",EDGE,"E11.left"),sQuery(id+"F0.wireOp",EDGE,"E11.right"),sQuery(id+"F0.wireOp",EDGE,"E29.bottom"),sQuery(id+"F0.wireOp",EDGE,"E29.top")])]});
            var Q20;
            Q20=makeQuery(id+"F4.opExtrude","SWEPT_BODY",BODY,{"disambiguationData":[OSD([sQuery(id+"F0.wireOp",EDGE,"E17.4.0.2"),sQuery(id+"F0.wireOp",EDGE,"E22"),sQuery(id+"F0.wireOp",EDGE,"E23"),sQuery(id+"F0.wireOp",EDGE,"E24")])]});
            var Q21;
            Q21=makeQuery(id+"F3.opExtrude","SWEPT_BODY",BODY,{"disambiguationData":[OSD([sQuery(id+"F0.wireOp",EDGE,"E17.4.0.0"),sQuery(id+"F0.wireOp",EDGE,"E17.4.0.2"),sQuery(id+"F0.wireOp",EDGE,"E22"),sQuery(id+"F0.wireOp",EDGE,"E24"),sQuery(id+"F0.wireOp",EDGE,"E80.trimOffspring")])]});
            var Q22;
            Q22=makeQuery(id+"F3.opExtrude","SWEPT_BODY",BODY,{"disambiguationData":[OSD([sQuery(id+"F0.wireOp",EDGE,"E17.3.0.0"),sQuery(id+"F0.wireOp",EDGE,"E17.3.0.2"),sQuery(id+"F0.wireOp",EDGE,"E22"),sQuery(id+"F0.wireOp",EDGE,"E80.trimOffspring")])]});
            var Q23;
            Q23=makeQuery(id+"F4.opExtrude","SWEPT_BODY",BODY,{"disambiguationData":[OSD([sQuery(id+"F0.wireOp",EDGE,"E17.3.0.2"),sQuery(id+"F0.wireOp",EDGE,"E17.4.0.0"),sQuery(id+"F0.wireOp",EDGE,"E22"),sQuery(id+"F0.wireOp",EDGE,"E80.trimOffspring")])]});
            var Q24;
            Q24=makeQuery(id+"F4.opExtrude","SWEPT_BODY",BODY,{"disambiguationData":[OSD([sQuery(id+"F0.wireOp",EDGE,"E15.1.0.2"),sQuery(id+"F0.wireOp",EDGE,"E15.2.0.0"),sQuery(id+"F0.wireOp",EDGE,"E22"),sQuery(id+"F0.wireOp",EDGE,"E80.trimOffspring")])]});
            var Q25;
            Q25=makeQuery(id+"F4.opExtrude","SWEPT_BODY",BODY,{"disambiguationData":[OSD([sQuery(id+"F0.wireOp",EDGE,"E15.2.0.2"),sQuery(id+"F0.wireOp",EDGE,"E15.3.0.0"),sQuery(id+"F0.wireOp",EDGE,"E22"),sQuery(id+"F0.wireOp",EDGE,"E80.trimOffspring")])]});
            var Q26;
            Q26=makeQuery(id+"F4.opExtrude","SWEPT_BODY",BODY,{"disambiguationData":[OSD([sQuery(id+"F0.wireOp",EDGE,"E15.3.0.2"),sQuery(id+"F0.wireOp",EDGE,"E16.left"),sQuery(id+"F0.wireOp",EDGE,"E22"),sQuery(id+"F0.wireOp",EDGE,"E80.trimOffspring")])]});
            var Q27;
            Q27=makeQuery(id+"F4.opExtrude","SWEPT_BODY",BODY,{"disambiguationData":[OSD([sQuery(id+"F0.wireOp",EDGE,"E17.1.0.2"),sQuery(id+"F0.wireOp",EDGE,"E17.2.0.0"),sQuery(id+"F0.wireOp",EDGE,"E22"),sQuery(id+"F0.wireOp",EDGE,"E80.trimOffspring")])]});
            var Q28;
            Q28=makeQuery(id+"F4.opExtrude","SWEPT_BODY",BODY,{"disambiguationData":[OSD([sQuery(id+"F0.wireOp",EDGE,"E17.2.0.2"),sQuery(id+"F0.wireOp",EDGE,"E17.3.0.0"),sQuery(id+"F0.wireOp",EDGE,"E22"),sQuery(id+"F0.wireOp",EDGE,"E80.trimOffspring")])]});
            var Q29;
            Q29=makeQuery(id+"F4.opExtrude","SWEPT_BODY",BODY,{"disambiguationData":[OSD([sQuery(id+"F0.wireOp",EDGE,"E17.3.0.2"),sQuery(id+"F0.wireOp",EDGE,"E17.4.0.0"),sQuery(id+"F0.wireOp",EDGE,"E22"),sQuery(id+"F0.wireOp",EDGE,"E80.trimOffspring")])]});
            var Q30;
            Q30=makeQuery(id+"F4.opExtrude","SWEPT_BODY",BODY,{"disambiguationData":[OSD([sQuery(id+"F0.wireOp",EDGE,"E17.4.0.2"),sQuery(id+"F0.wireOp",EDGE,"E22"),sQuery(id+"F0.wireOp",EDGE,"E23"),sQuery(id+"F0.wireOp",EDGE,"E24")])]});
            var Q31;
            Q31=makeQuery(id+"F4.opExtrude","SWEPT_BODY",BODY,{"disambiguationData":[OSD([sQuery(id+"F0.wireOp",EDGE,"E9.1.0.3"),sQuery(id+"F0.wireOp",EDGE,"E9.2.0.1"),sQuery(id+"F0.wireOp",EDGE,"E25"),sQuery(id+"F0.wireOp",EDGE,"E26")])]});
            var Q32;
            Q32=makeQuery(id+"F4.opExtrude","SWEPT_BODY",BODY,{"disambiguationData":[OSD([sQuery(id+"F0.wireOp",EDGE,"E8.right"),sQuery(id+"F0.wireOp",EDGE,"E9.1.0.1"),sQuery(id+"F0.wireOp",EDGE,"E25"),sQuery(id+"F0.wireOp",EDGE,"E26")])]});
            var Q33;
            Q33=makeQuery(id+"F4.opExtrude","SWEPT_BODY",BODY,{"disambiguationData":[OSD([sQuery(id+"F0.wireOp",EDGE,"E8.left"),sQuery(id+"F0.wireOp",EDGE,"E26"),sQuery(id+"F0.wireOp",EDGE,"E30"),sQuery(id+"F0.wireOp",EDGE,"E35")])]});
            var Q34;
            Q34=makeQuery(id+"F4.opExtrude","SWEPT_BODY",BODY,{"disambiguationData":[OSD([sQuery(id+"F0.wireOp",EDGE,"E15.1.0.2"),sQuery(id+"F0.wireOp",EDGE,"E15.2.0.0"),sQuery(id+"F0.wireOp",EDGE,"E22"),sQuery(id+"F0.wireOp",EDGE,"E80.trimOffspring")])]});
            var Q35;
            Q35=makeQuery(id+"F4.opExtrude","SWEPT_BODY",BODY,{"disambiguationData":[OSD([sQuery(id+"F0.wireOp",EDGE,"E15.2.0.2"),sQuery(id+"F0.wireOp",EDGE,"E15.3.0.0"),sQuery(id+"F0.wireOp",EDGE,"E22"),sQuery(id+"F0.wireOp",EDGE,"E80.trimOffspring")])]});
            var Q36;
            Q36=makeQuery(id+"F4.opExtrude","SWEPT_BODY",BODY,{"disambiguationData":[OSD([sQuery(id+"F0.wireOp",EDGE,"E15.3.0.2"),sQuery(id+"F0.wireOp",EDGE,"E16.left"),sQuery(id+"F0.wireOp",EDGE,"E22"),sQuery(id+"F0.wireOp",EDGE,"E80.trimOffspring")])]});
            var Q37;
            Q37=makeQuery(id+"F4.opExtrude","SWEPT_BODY",BODY,{"disambiguationData":[OSD([sQuery(id+"F0.wireOp",EDGE,"E17.1.0.2"),sQuery(id+"F0.wireOp",EDGE,"E17.2.0.0"),sQuery(id+"F0.wireOp",EDGE,"E22"),sQuery(id+"F0.wireOp",EDGE,"E80.trimOffspring")])]});
            var Q38;
            Q38=makeQuery(id+"F4.opExtrude","SWEPT_BODY",BODY,{"disambiguationData":[OSD([sQuery(id+"F0.wireOp",EDGE,"E17.2.0.2"),sQuery(id+"F0.wireOp",EDGE,"E17.3.0.0"),sQuery(id+"F0.wireOp",EDGE,"E22"),sQuery(id+"F0.wireOp",EDGE,"E80.trimOffspring")])]});
            var Q39;
            Q39=makeQuery(id+"F4.opExtrude","SWEPT_BODY",BODY,{"disambiguationData":[OSD([sQuery(id+"F0.wireOp",EDGE,"E17.3.0.2"),sQuery(id+"F0.wireOp",EDGE,"E17.4.0.0"),sQuery(id+"F0.wireOp",EDGE,"E22"),sQuery(id+"F0.wireOp",EDGE,"E80.trimOffspring")])]});
            var Q40;
            Q40=makeQuery(id+"F4.opExtrude","SWEPT_BODY",BODY,{"disambiguationData":[OSD([sQuery(id+"F0.wireOp",EDGE,"E17.4.0.2"),sQuery(id+"F0.wireOp",EDGE,"E22"),sQuery(id+"F0.wireOp",EDGE,"E23"),sQuery(id+"F0.wireOp",EDGE,"E24")])]});
            var Q41;
            Q41=makeQuery(id+"F3.opExtrude","SWEPT_BODY",BODY,{"disambiguationData":[OSD([sQuery(id+"F0.wireOp",EDGE,"E9.1.0.1"),sQuery(id+"F0.wireOp",EDGE,"E9.1.0.3"),sQuery(id+"F0.wireOp",EDGE,"E25"),sQuery(id+"F0.wireOp",EDGE,"E26")])]});
            var Q42;
            Q42=makeQuery(id+"F3.opExtrude","SWEPT_BODY",BODY,{"disambiguationData":[OSD([sQuery(id+"F0.wireOp",EDGE,"E8.left"),sQuery(id+"F0.wireOp",EDGE,"E8.right"),sQuery(id+"F0.wireOp",EDGE,"E25"),sQuery(id+"F0.wireOp",EDGE,"E26")])]});
            var Q43;
            Q43=makeQuery(id+"F4.opExtrude","SWEPT_BODY",BODY,{"disambiguationData":[OSD([sQuery(id+"F0.wireOp",EDGE,"E15.1.0.2"),sQuery(id+"F0.wireOp",EDGE,"E15.2.0.0"),sQuery(id+"F0.wireOp",EDGE,"E22"),sQuery(id+"F0.wireOp",EDGE,"E80.trimOffspring")])]});
            var Q44;
            Q44=makeQuery(id+"F4.opExtrude","SWEPT_BODY",BODY,{"disambiguationData":[OSD([sQuery(id+"F0.wireOp",EDGE,"E15.2.0.2"),sQuery(id+"F0.wireOp",EDGE,"E15.3.0.0"),sQuery(id+"F0.wireOp",EDGE,"E22"),sQuery(id+"F0.wireOp",EDGE,"E80.trimOffspring")])]});
            var Q45;
            Q45=makeQuery(id+"F3.opExtrude","SWEPT_BODY",BODY,{"disambiguationData":[OSD([sQuery(id+"F0.wireOp",EDGE,"E16.left"),sQuery(id+"F0.wireOp",EDGE,"E16.right"),sQuery(id+"F0.wireOp",EDGE,"E22"),sQuery(id+"F0.wireOp",EDGE,"E80.trimOffspring")])]});
            var Q46;
            Q46=makeQuery(id+"F3.opExtrude","SWEPT_BODY",BODY,{"disambiguationData":[OSD([sQuery(id+"F0.wireOp",EDGE,"E15.1.0.2"),sQuery(id+"F0.wireOp",EDGE,"E22"),sQuery(id+"F0.wireOp",EDGE,"E80.trimOffspring"),sQuery(id+"F0.wireOp",EDGE,"a3QPaEm2-lXkB-GlV2-W4xq-NRGzucZuLk07")])]});
            var Q47;
            Q47=makeQuery(id+"F3.opExtrude","SWEPT_BODY",BODY,{"disambiguationData":[OSD([sQuery(id+"F0.wireOp",EDGE,"E15.2.0.0"),sQuery(id+"F0.wireOp",EDGE,"E15.2.0.2"),sQuery(id+"F0.wireOp",EDGE,"E22"),sQuery(id+"F0.wireOp",EDGE,"E80.trimOffspring")])]});
            var Q48;
            Q48=makeQuery(id+"F3.opExtrude","SWEPT_BODY",BODY,{"disambiguationData":[OSD([sQuery(id+"F0.wireOp",EDGE,"E15.3.0.0"),sQuery(id+"F0.wireOp",EDGE,"E15.3.0.2"),sQuery(id+"F0.wireOp",EDGE,"E22"),sQuery(id+"F0.wireOp",EDGE,"E80.trimOffspring")])]});
            var Q49;
            Q49=makeQuery(id+"F3.opExtrude","SWEPT_BODY",BODY,{"disambiguationData":[OSD([sQuery(id+"F0.wireOp",EDGE,"E16.left"),sQuery(id+"F0.wireOp",EDGE,"E16.right"),sQuery(id+"F0.wireOp",EDGE,"E22"),sQuery(id+"F0.wireOp",EDGE,"E80.trimOffspring")])]});
            var Q50;
            Q50=makeQuery(id+"F3.opExtrude","SWEPT_BODY",BODY,{"disambiguationData":[OSD([sQuery(id+"F0.wireOp",EDGE,"E17.2.0.0"),sQuery(id+"F0.wireOp",EDGE,"E17.2.0.2"),sQuery(id+"F0.wireOp",EDGE,"E22"),sQuery(id+"F0.wireOp",EDGE,"E80.trimOffspring")])]});
            var Q51;
            Q51=makeQuery(id+"F3.opExtrude","SWEPT_BODY",BODY,{"disambiguationData":[OSD([sQuery(id+"F0.wireOp",EDGE,"E17.3.0.0"),sQuery(id+"F0.wireOp",EDGE,"E17.3.0.2"),sQuery(id+"F0.wireOp",EDGE,"E22"),sQuery(id+"F0.wireOp",EDGE,"E80.trimOffspring")])]});
            var Q52;
            Q52=makeQuery(id+"F3.opExtrude","SWEPT_BODY",BODY,{"disambiguationData":[OSD([sQuery(id+"F0.wireOp",EDGE,"E9.2.0.1"),sQuery(id+"F0.wireOp",EDGE,"E9.2.0.3"),sQuery(id+"F0.wireOp",EDGE,"E25"),sQuery(id+"F0.wireOp",EDGE,"E26")])]});
            var Q53;
            Q53=makeQuery(id+"F3.opExtrude","SWEPT_BODY",BODY,{"disambiguationData":[OSD([sQuery(id+"F0.wireOp",EDGE,"E17.2.0.0"),sQuery(id+"F0.wireOp",EDGE,"E17.2.0.2"),sQuery(id+"F0.wireOp",EDGE,"E22"),sQuery(id+"F0.wireOp",EDGE,"E80.trimOffspring")])]});
            var Q54;
            Q54=makeQuery(id+"F3.opExtrude","SWEPT_BODY",BODY,{"disambiguationData":[OSD([sQuery(id+"F0.wireOp",EDGE,"E15.2.0.0"),sQuery(id+"F0.wireOp",EDGE,"E15.2.0.2"),sQuery(id+"F0.wireOp",EDGE,"E22"),sQuery(id+"F0.wireOp",EDGE,"E80.trimOffspring")])]});
            var Q55;
            Q55=makeQuery(id+"F3.opExtrude","SWEPT_BODY",BODY,{"disambiguationData":[OSD([sQuery(id+"F0.wireOp",EDGE,"E15.1.0.2"),sQuery(id+"F0.wireOp",EDGE,"E22"),sQuery(id+"F0.wireOp",EDGE,"E80.trimOffspring"),sQuery(id+"F0.wireOp",EDGE,"a3QPaEm2-lXkB-GlV2-W4xq-NRGzucZuLk07")])]});
            var Q56;
            Q56=makeQuery(id+"F4.opExtrude","SWEPT_BODY",BODY,{"disambiguationData":[OSD([sQuery(id+"F0.wireOp",EDGE,"E17.1.0.2"),sQuery(id+"F0.wireOp",EDGE,"E17.2.0.0"),sQuery(id+"F0.wireOp",EDGE,"E22"),sQuery(id+"F0.wireOp",EDGE,"E80.trimOffspring")])]});
            var Q57;
            Q57=makeQuery(id+"F4.opExtrude","SWEPT_BODY",BODY,{"disambiguationData":[OSD([sQuery(id+"F0.wireOp",EDGE,"E17.2.0.2"),sQuery(id+"F0.wireOp",EDGE,"E17.3.0.0"),sQuery(id+"F0.wireOp",EDGE,"E22"),sQuery(id+"F0.wireOp",EDGE,"E80.trimOffspring")])]});
            var Q58;
            Q58=makeQuery(id+"F4.opExtrude","SWEPT_BODY",BODY,{"disambiguationData":[OSD([sQuery(id+"F0.wireOp",EDGE,"E14.1.0.1"),sQuery(id+"F0.wireOp",EDGE,"E27"),sQuery(id+"F0.wireOp",EDGE,"E28"),sQuery(id+"F0.wireOp",EDGE,"E31")])]});
            var Q59;
            Q59=makeQuery(id+"F3.opExtrude","SWEPT_BODY",BODY,{"disambiguationData":[OSD([sQuery(id+"F0.wireOp",EDGE,"E14.2.0.0"),sQuery(id+"F0.wireOp",EDGE,"E14.2.0.1"),sQuery(id+"F0.wireOp",EDGE,"E27"),sQuery(id+"F0.wireOp",EDGE,"E28")])]});
            var Q60;
            Q60=makeQuery(id+"F3.opExtrude","SWEPT_BODY",BODY,{"disambiguationData":[OSD([sQuery(id+"F0.wireOp",EDGE,"E14.1.0.0"),sQuery(id+"F0.wireOp",EDGE,"E14.1.0.1"),sQuery(id+"F0.wireOp",EDGE,"E27"),sQuery(id+"F0.wireOp",EDGE,"E28")])]});
            var Q61;
            Q61=makeQuery(id+"F4.opExtrude","SWEPT_BODY",BODY,{"disambiguationData":[OSD([sQuery(id+"F0.wireOp",EDGE,"E32"),sQuery(id+"F0.wireOp",EDGE,"E33"),sQuery(id+"F0.wireOp",EDGE,"E34"),sQuery(id+"F0.wireOp",EDGE,"E75")])]});
            var Q62;
            Q62=makeQuery(id+"F3.opExtrude","SWEPT_BODY",BODY,{"disambiguationData":[OSD([sQuery(id+"F0.wireOp",EDGE,"E32"),sQuery(id+"F0.wireOp",EDGE,"E34"),sQuery(id+"F0.wireOp",EDGE,"E74"),sQuery(id+"F0.wireOp",EDGE,"E75")])]});
            var Q63;
            Q63=makeQuery(id+"F4.opExtrude","SWEPT_BODY",BODY,{"disambiguationData":[OSD([sQuery(id+"F0.wireOp",EDGE,"E32"),sQuery(id+"F0.wireOp",EDGE,"E34"),sQuery(id+"F0.wireOp",EDGE,"E70"),sQuery(id+"F0.wireOp",EDGE,"E74")])]});
            var Q64;
            Q64=makeQuery(id+"F4.opExtrude","SWEPT_BODY",BODY,{"disambiguationData":[OSD([sQuery(id+"F0.wireOp",EDGE,"E32"),sQuery(id+"F0.wireOp",EDGE,"E33"),sQuery(id+"F0.wireOp",EDGE,"E34"),sQuery(id+"F0.wireOp",EDGE,"E75")])]});
            var Q65;
            Q65=makeQuery(id+"F4.opExtrude","SWEPT_BODY",BODY,{"disambiguationData":[OSD([sQuery(id+"F0.wireOp",EDGE,"E10.right"),sQuery(id+"F0.wireOp",EDGE,"E14.1.0.0"),sQuery(id+"F0.wireOp",EDGE,"E27"),sQuery(id+"F0.wireOp",EDGE,"E28")])]});
            var Q66;
            Q66=makeQuery(id+"F3.opExtrude","SWEPT_BODY",BODY,{"disambiguationData":[OSD([sQuery(id+"F0.wireOp",EDGE,"E10.left"),sQuery(id+"F0.wireOp",EDGE,"E10.right"),sQuery(id+"F0.wireOp",EDGE,"E27"),sQuery(id+"F0.wireOp",EDGE,"E28")])]});
            var Q67;
            Q67=makeQuery(id+"F4.opExtrude","SWEPT_BODY",BODY,{"disambiguationData":[OSD([sQuery(id+"F0.wireOp",EDGE,"E10.left"),sQuery(id+"F0.wireOp",EDGE,"E27"),sQuery(id+"F0.wireOp",EDGE,"E28"),sQuery(id+"F0.wireOp",EDGE,"E67")])]});
            var Q68;
            Q68=makeQuery(id+"F5.opExtrude","SWEPT_BODY",BODY,{"disambiguationData":[OSD([sQuery(id+"F0.wireOp",EDGE,"E21.left"),sQuery(id+"F0.wireOp",EDGE,"E73.bottom"),sQuery(id+"F0.wireOp",EDGE,"E73.top"),sQuery(id+"F0.wireOp",EDGE,"E73.right")])]});
            var Q69;
            Q69=makeQuery(id+"F5.opExtrude","SWEPT_BODY",BODY,{"disambiguationData":[OSD([sQuery(id+"F0.wireOp",EDGE,"E20.right"),sQuery(id+"F0.wireOp",EDGE,"E72.bottom"),sQuery(id+"F0.wireOp",EDGE,"E72.top"),sQuery(id+"F0.wireOp",EDGE,"E72.left")])]});
            var Q70;
            Q70=makeQuery(id+"F3.opExtrude","SWEPT_BODY",BODY,{"disambiguationData":[OSD([sQuery(id+"F0.wireOp",EDGE,"E21.left"),sQuery(id+"F0.wireOp",EDGE,"E21.right"),sQuery(id+"F0.wireOp",EDGE,"E73.bottom"),sQuery(id+"F0.wireOp",EDGE,"E73.top")])]});
            var Q71;
            Q71=makeQuery(id+"F5.opExtrude","SWEPT_BODY",BODY,{"disambiguationData":[OSD([sQuery(id+"F0.wireOp",EDGE,"E21.right"),sQuery(id+"F0.wireOp",EDGE,"E73.bottom"),sQuery(id+"F0.wireOp",EDGE,"E73.top"),sQuery(id+"F0.wireOp",EDGE,"E73.left")])]});
            var Q72;
            Q72=makeQuery(id+"F3.opExtrude","SWEPT_BODY",BODY,{"disambiguationData":[OSD([sQuery(id+"F0.wireOp",EDGE,"E20.left"),sQuery(id+"F0.wireOp",EDGE,"E20.right"),sQuery(id+"F0.wireOp",EDGE,"E72.bottom"),sQuery(id+"F0.wireOp",EDGE,"E72.top")])]});
            var Q73;
            Q73=makeQuery(id+"F5.opExtrude","SWEPT_BODY",BODY,{"disambiguationData":[OSD([sQuery(id+"F0.wireOp",EDGE,"E20.left"),sQuery(id+"F0.wireOp",EDGE,"E72.bottom"),sQuery(id+"F0.wireOp",EDGE,"E72.top"),sQuery(id+"F0.wireOp",EDGE,"E72.right")])]});
            var Q74;
            Q74=makeQuery(id+"F3.opExtrude","SWEPT_BODY",BODY,{"disambiguationData":[OSD([sQuery(id+"F0.wireOp",EDGE,"E15.1.0.2"),sQuery(id+"F0.wireOp",EDGE,"E22"),sQuery(id+"F0.wireOp",EDGE,"E80.trimOffspring"),sQuery(id+"F0.wireOp",EDGE,"a3QPaEm2-lXkB-GlV2-W4xq-NRGzucZuLk07")])]});
            var Q75;
            Q75=makeQuery(id+"F3.opExtrude","SWEPT_BODY",BODY,{"disambiguationData":[OSD([sQuery(id+"F0.wireOp",EDGE,"E15.2.0.0"),sQuery(id+"F0.wireOp",EDGE,"E15.2.0.2"),sQuery(id+"F0.wireOp",EDGE,"E22"),sQuery(id+"F0.wireOp",EDGE,"E80.trimOffspring")])]});
            var Q76;
            Q76=makeQuery(id+"F3.opExtrude","SWEPT_BODY",BODY,{"disambiguationData":[OSD([sQuery(id+"F0.wireOp",EDGE,"E15.3.0.0"),sQuery(id+"F0.wireOp",EDGE,"E15.3.0.2"),sQuery(id+"F0.wireOp",EDGE,"E22"),sQuery(id+"F0.wireOp",EDGE,"E80.trimOffspring")])]});
            var Q77;
            Q77=makeQuery(id+"F3.opExtrude","SWEPT_BODY",BODY,{"disambiguationData":[OSD([sQuery(id+"F0.wireOp",EDGE,"E16.left"),sQuery(id+"F0.wireOp",EDGE,"E16.right"),sQuery(id+"F0.wireOp",EDGE,"E22"),sQuery(id+"F0.wireOp",EDGE,"E80.trimOffspring")])]});
            var Q78;
            Q78=makeQuery(id+"F3.opExtrude","SWEPT_BODY",BODY,{"disambiguationData":[OSD([sQuery(id+"F0.wireOp",EDGE,"E17.2.0.0"),sQuery(id+"F0.wireOp",EDGE,"E17.2.0.2"),sQuery(id+"F0.wireOp",EDGE,"E22"),sQuery(id+"F0.wireOp",EDGE,"E80.trimOffspring")])]});
            var Q79;
            Q79=makeQuery(id+"F3.opExtrude","SWEPT_BODY",BODY,{"disambiguationData":[OSD([sQuery(id+"F0.wireOp",EDGE,"E17.3.0.0"),sQuery(id+"F0.wireOp",EDGE,"E17.3.0.2"),sQuery(id+"F0.wireOp",EDGE,"E22"),sQuery(id+"F0.wireOp",EDGE,"E80.trimOffspring")])]});
            var Q80;
            Q80=makeQuery(id+"F4.opExtrude","SWEPT_BODY",BODY,{"disambiguationData":[OSD([sQuery(id+"F0.wireOp",EDGE,"E15.3.0.2"),sQuery(id+"F0.wireOp",EDGE,"E16.left"),sQuery(id+"F0.wireOp",EDGE,"E22"),sQuery(id+"F0.wireOp",EDGE,"E80.trimOffspring")])]});
            var Q81;
            Q81=makeQuery(id+"F5.opExtrude","SWEPT_BODY",BODY,{"disambiguationData":[OSD([sQuery(id+"F0.wireOp",EDGE,"E17.2.0.0"),sQuery(id+"F0.wireOp",EDGE,"E22"),sQuery(id+"F0.wireOp",EDGE,"E80.trimOffspring"),sQuery(id+"F0.wireOp",EDGE,"E85")])]});
            booleanBodies(context, id + "F6", {"operationType" : BooleanOperationType.UNION, "tools" : qUnion([Q0, Q1, Q2, Q3, Q4, Q5, Q6, Q7, Q8, Q9, Q10, Q11, Q12, Q13, Q14, Q15, Q16, Q17, Q18, Q19, Q20, Q21, Q22, Q23, Q24, Q25, Q26, Q27, Q28, Q29, Q30, Q31, Q32, Q33, Q34, Q35, Q36, Q37, Q38, Q39, Q40, Q41, Q42, Q43, Q44, Q45, Q46, Q47, Q48, Q49, Q50, Q51, Q52, Q53, Q54, Q55, Q56, Q57, Q58, Q59, Q60, Q61, Q62, Q63, Q64, Q65, Q66, Q67, Q68, Q69, Q70, Q71, Q72, Q73, Q74, Q75, Q76, Q77, Q78, Q79, Q80, Q81])});
        }
        {
            var Q0;
            Q0=makeQuery(id+"F3.opExtrude","SWEPT_BODY",BODY,{"disambiguationData":[OSD([sQuery(id+"F0.wireOp",EDGE,"E83"),sQuery(id+"F0.wireOp",EDGE,"E15.3.0.0"),sQuery(id+"F0.wireOp",EDGE,"E15.3.0.2"),sQuery(id+"F0.wireOp",EDGE,"E22")])]});
            var Q1;
            Q1=makeQuery(id+"F4.opExtrude","SWEPT_BODY",BODY,{"disambiguationData":[OSD([sQuery(id+"F0.wireOp",EDGE,"E17.4.0.2"),sQuery(id+"F0.wireOp",EDGE,"E22"),sQuery(id+"F0.wireOp",EDGE,"E23"),sQuery(id+"F0.wireOp",EDGE,"E24")])]});
            var Q2;
            Q2=makeQuery(id+"F3.opExtrude","SWEPT_BODY",BODY,{"disambiguationData":[OSD([sQuery(id+"F0.wireOp",EDGE,"E20.bottom"),sQuery(id+"F0.wireOp",EDGE,"E20.top"),sQuery(id+"F0.wireOp",EDGE,"E20.left"),sQuery(id+"F0.wireOp",EDGE,"E20.right")])]});
            var Q3;
            Q3=makeQuery(id+"F3.opExtrude","SWEPT_BODY",BODY,{"disambiguationData":[OSD([sQuery(id+"F0.wireOp",EDGE,"E21.bottom"),sQuery(id+"F0.wireOp",EDGE,"E21.top"),sQuery(id+"F0.wireOp",EDGE,"E21.left"),sQuery(id+"F0.wireOp",EDGE,"E21.right")])]});
            var Q4;
            Q4=makeQuery(id+"F4.opExtrude","SWEPT_BODY",BODY,{"disambiguationData":[OSD([sQuery(id+"F0.wireOp",EDGE,"E13.left"),sQuery(id+"F0.wireOp",EDGE,"E32"),sQuery(id+"F0.wireOp",EDGE,"E33"),sQuery(id+"F0.wireOp",EDGE,"E34")])]});
            var Q5;
            Q5=makeQuery(id+"F4.opExtrude","SWEPT_BODY",BODY,{"disambiguationData":[OSD([sQuery(id+"F0.wireOp",EDGE,"E11.right"),sQuery(id+"F0.wireOp",EDGE,"E12.1.0.0"),sQuery(id+"F0.wireOp",EDGE,"E29.bottom"),sQuery(id+"F0.wireOp",EDGE,"E29.top")])]});
            var Q6;
            Q6=makeQuery(id+"F4.opExtrude","SWEPT_BODY",BODY,{"disambiguationData":[OSD([sQuery(id+"F0.wireOp",EDGE,"E9.1.0.3"),sQuery(id+"F0.wireOp",EDGE,"E9.2.0.1"),sQuery(id+"F0.wireOp",EDGE,"E25"),sQuery(id+"F0.wireOp",EDGE,"E26")])]});
            var Q7;
            Q7=makeQuery(id+"F4.opExtrude","SWEPT_BODY",BODY,{"disambiguationData":[OSD([sQuery(id+"F0.wireOp",EDGE,"E14.1.0.1"),sQuery(id+"F0.wireOp",EDGE,"E27"),sQuery(id+"F0.wireOp",EDGE,"E28"),sQuery(id+"F0.wireOp",EDGE,"E31")])]});
            var Q8;
            Q8=makeQuery(id+"F5.opExtrude","SWEPT_BODY",BODY,{"disambiguationData":[OSD([sQuery(id+"F0.wireOp",EDGE,"E21.left"),sQuery(id+"F0.wireOp",EDGE,"E73.bottom"),sQuery(id+"F0.wireOp",EDGE,"E73.top"),sQuery(id+"F0.wireOp",EDGE,"E73.right")])]});
            var Q9;
            Q9=makeQuery(id+"F5.opExtrude","SWEPT_BODY",BODY,{"disambiguationData":[OSD([sQuery(id+"F0.wireOp",EDGE,"E20.right"),sQuery(id+"F0.wireOp",EDGE,"E72.bottom"),sQuery(id+"F0.wireOp",EDGE,"E72.top"),sQuery(id+"F0.wireOp",EDGE,"E72.left")])]});
            var Q10;
            Q10=makeQuery(id+"F4.opExtrude","SWEPT_BODY",BODY,{"disambiguationData":[OSD([sQuery(id+"F0.wireOp",EDGE,"E16.right"),sQuery(id+"F0.wireOp",EDGE,"E22"),sQuery(id+"F0.wireOp",EDGE,"E80.trimOffspring"),sQuery(id+"F0.wireOp",EDGE,"E86")])]});
            var Q11;
            Q11=makeQuery(id+"F4.opExtrude","SWEPT_BODY",BODY,{"disambiguationData":[OSD([sQuery(id+"F0.wireOp",EDGE,"E17.1.0.2"),sQuery(id+"F0.wireOp",EDGE,"E17.2.0.0"),sQuery(id+"F0.wireOp",EDGE,"E22"),sQuery(id+"F0.wireOp",EDGE,"E80.trimOffspring")])]});
            var Q12;
            Q12=makeQuery(id+"F5.opExtrude","SWEPT_BODY",BODY,{"disambiguationData":[OSD([sQuery(id+"F0.wireOp",EDGE,"E17.2.0.0"),sQuery(id+"F0.wireOp",EDGE,"E22"),sQuery(id+"F0.wireOp",EDGE,"E80.trimOffspring"),sQuery(id+"F0.wireOp",EDGE,"E85")])]});
            var Q13;
            Q13=makeQuery(id+"F3.opExtrude","SWEPT_BODY",BODY,{"disambiguationData":[OSD([sQuery(id+"F0.wireOp",EDGE,"E22"),sQuery(id+"F0.wireOp",EDGE,"E80.trimOffspring"),sQuery(id+"F0.wireOp",EDGE,"E85"),sQuery(id+"F0.wireOp",EDGE,"E86")])]});
            var Q14;
            {var subQ0=sQuery(id+"F0.wireOp",EDGE,"E22");var subQ1=sQuery(id+"F0.wireOp",EDGE,"E15.3.0.0");var subQ2=sQuery(id+"F0.wireOp",EDGE,"E15.2.0.2");var subQ3=sQuery(id+"F0.wireOp",EDGE,"E83");var subQ4=sQuery(id+"F0.wireOp",EDGE,"E15.2.0.0");var subQ5=sQuery(id+"F0.wireOp",EDGE,"E15.1.0.2");var subQ6=sQuery(id+"F0.wireOp",EDGE,"E15.1.0.0");var subQ7=sQuery(id+"F0.wireOp",EDGE,"E84.right");var subQ8=sQuery(id+"F0.wireOp",EDGE,"E84.left");Q14=makeQuery(id+"F6.opBoolean","MERGE",FACE,{"derivedFrom":[makeQuery(id+"F3.opExtrude","CAP_FACE",FACE,{"disambiguationData":[OSD([subQ3,subQ6,subQ5,subQ0])],"isStart":false}),makeQuery(id+"F3.opExtrude","CAP_FACE",FACE,{"disambiguationData":[OSD([subQ3,subQ4,subQ2,subQ0])],"isStart":false}),makeQuery(id+"F3.opExtrude","CAP_FACE",FACE,{"disambiguationData":[OSD([subQ3,subQ1,sQuery(id+"F0.wireOp",EDGE,"E15.3.0.2"),subQ0])],"isStart":false}),makeQuery(id+"F3.opExtrude","CAP_FACE",FACE,{"disambiguationData":[OSD([sQuery(id+"F0.wireOp",EDGE,"E84.bottom"),subQ8,subQ7,subQ0])],"isStart":false}),makeQuery(id+"F4.opExtrude","CAP_FACE",FACE,{"disambiguationData":[OSD([subQ3,sQuery(id+"F0.wireOp",EDGE,"E6"),subQ8,subQ0])],"isStart":false}),makeQuery(id+"F4.opExtrude","CAP_FACE",FACE,{"disambiguationData":[OSD([subQ3,subQ7,subQ6,subQ0])],"isStart":false}),makeQuery(id+"F4.opExtrude","CAP_FACE",FACE,{"disambiguationData":[OSD([subQ3,subQ5,subQ4,subQ0])],"isStart":false}),makeQuery(id+"F4.opExtrude","CAP_FACE",FACE,{"disambiguationData":[OSD([subQ3,subQ2,subQ1,subQ0])],"isStart":false})]});}
            mirror(context, id + "F7", {"entities" : qUnion([Q0, Q1, Q2, Q3, Q4, Q5, Q6, Q7, Q8, Q9, Q10, Q11, Q12, Q13]), "mirrorPlane" : qUnion([Q14])});
        }
    });
